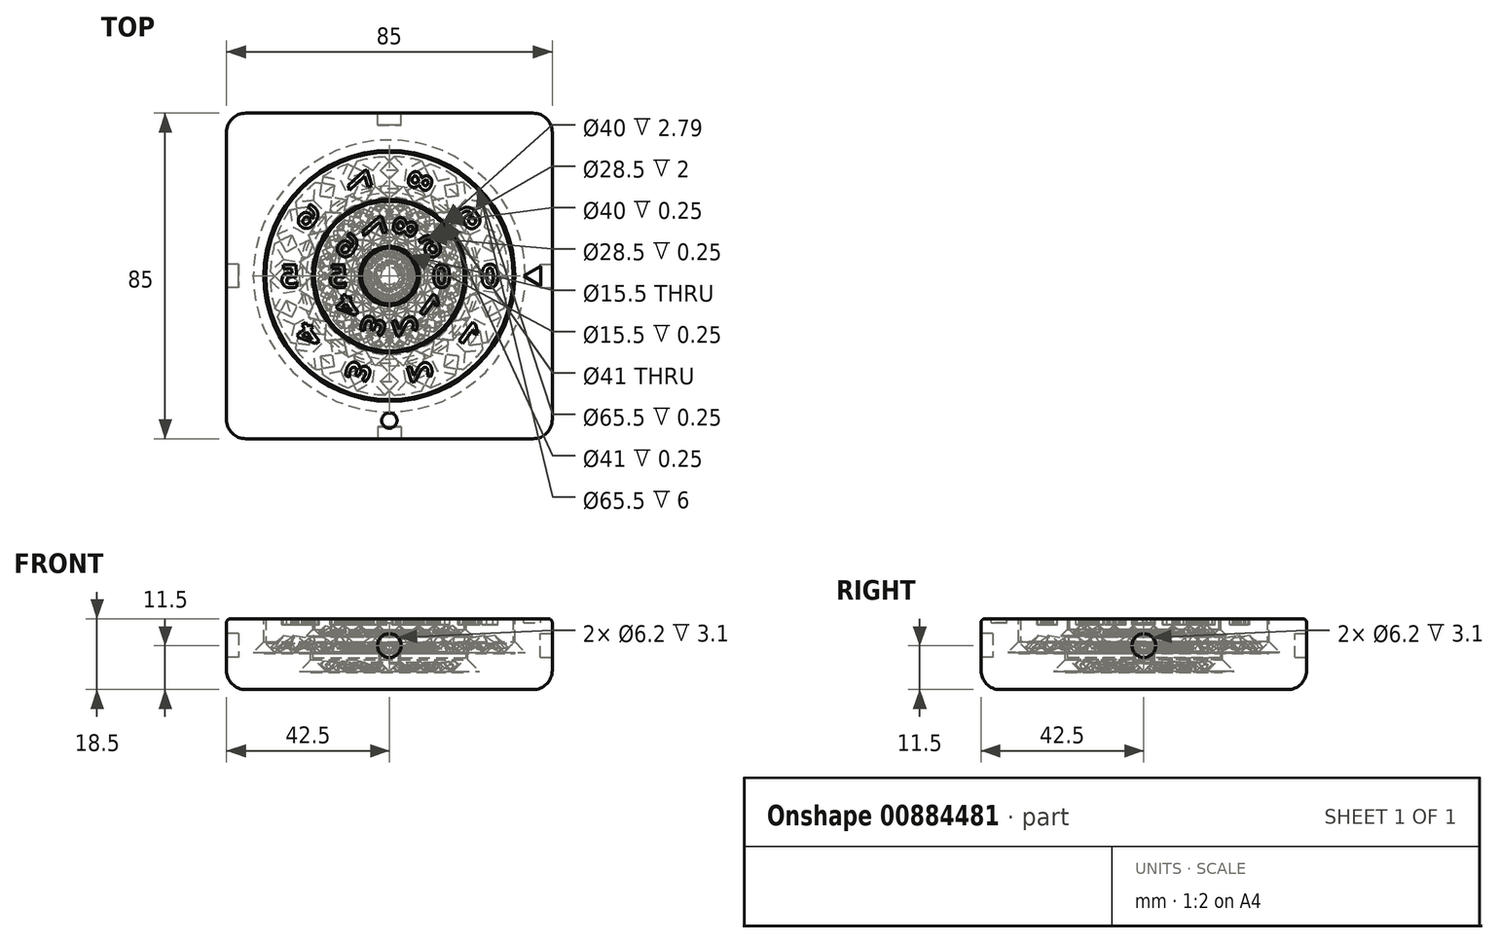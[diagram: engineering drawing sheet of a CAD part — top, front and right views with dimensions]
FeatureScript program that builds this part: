
annotation { "Feature Type Name" : "Feature", "Feature Type Description" : "" }
export const myFeature = defineFeature(function(context is Context, id is Id, definition is map)
    precondition{}
    {
        {
            var Q0;
            Q0=qCreatedBy(makeId("Top.planeOp"),FACE);
            var sketch = newSketch(context, id + "F0", { "sketchPlane" : qUnion([Q0])});
            skLineSegment(sketch, "E0.bottom", {"start": v(-42.5, 42.5) * mm, "end": v(42.5, 42.5) * mm});
            skLineSegment(sketch, "E0.top", {"start": v(-42.5, -42.5) * mm, "end": v(42.5, -42.5) * mm});
            skLineSegment(sketch, "E0.left", {"start": v(-42.5, 42.5) * mm, "end": v(-42.5, -42.5) * mm});
            skLineSegment(sketch, "E0.right", {"start": v(42.5, 42.5) * mm, "end": v(42.5, -42.5) * mm});
            skLineSegment(sketch, "E1", {"start": v(-42.5, 0) * mm, "end": v(42.5, 0) * mm, "construction": true});
            skLineSegment(sketch, "E2", {"start": v(0, -42.5) * mm, "end": v(0, 42.5) * mm, "construction": true});
            skCircle(sketch, "E3", {"center": v(0, -37.75) * mm, "radius": 2 * mm});
            skCircle(sketch, "E4", {"center": v(0, 0) * mm, "radius": 32.75 * mm});
            skCircle(sketch, "E5", {"center": v(0, 0) * mm, "radius": 20.5 * mm});
            skSolve(sketch);
        }
        {
            assignVariable(context, id + "F1", {"name" : "h", "anyValue" : 18.5});
        }
        {
            assignVariable(context, id + "F2", {"name" : "d", "anyValue" : 14});
        }
        {
            var Q0;
            Q0=makeQuery(id+"F0.imprint","IMPRINT",FACE,{"disambiguationData":[TD([[makeQuery(id+"F0.imprint","IMPRINT",EDGE,{"derivedFrom":sQuery(id+"F0.wireOp",EDGE,"TAnjNuv1-8zZz-IdIO-9YnW-rZbYslCo22iK.bottom")}),-1.0]])]});
            var Q1;
            Q1=makeQuery(id+"F0.imprint","IMPRINT",FACE,{"disambiguationData":[TD([[makeQuery(id+"F0.imprint","IMPRINT",EDGE,{"derivedFrom":sQuery(id+"F0.wireOp",EDGE,"E0.bottom")}),-1.0]])]});
            var Q2;
            Q2=makeQuery(id+"F0.imprint","IMPRINT",FACE,{"disambiguationData":[TD([[makeQuery(id+"F0.imprint","IMPRINT",EDGE,{"derivedFrom":sQuery(id+"F0.wireOp",EDGE,"2ee7e992-b2ee-4d81-b33c-59d4d4482344.0.2.0")}),1.0]])]});
            var Q3;
            Q3=makeQuery(id+"F0.imprint","IMPRINT",FACE,{"disambiguationData":[TD([[makeQuery(id+"F0.imprint","IMPRINT",EDGE,{"derivedFrom":sQuery(id+"F0.wireOp",EDGE,"2ee7e992-b2ee-4d81-b33c-59d4d4482344.0.3.0")}),1.0]])]});
            var Q4;
            Q4=makeQuery(id+"F0.imprint","IMPRINT",FACE,{"disambiguationData":[TD([[makeQuery(id+"F0.imprint","IMPRINT",EDGE,{"derivedFrom":sQuery(id+"F0.wireOp",EDGE,"2ee7e992-b2ee-4d81-b33c-59d4d4482344.0.1.0")}),1.0]])]});
            var Q5;
            Q5=makeQuery(id+"F0.imprint","IMPRINT",FACE,{"disambiguationData":[TD([[makeQuery(id+"F0.imprint","IMPRINT",EDGE,{"derivedFrom":sQuery(id+"F0.wireOp",EDGE,"f406dc69-17c4-4892-9ae8-b8d3958ef0eb.0.1.2")}),1.0]])]});
            var Q6;
            Q6=makeQuery(id+"F0.imprint","IMPRINT",FACE,{"disambiguationData":[TD([[makeQuery(id+"F0.imprint","IMPRINT",EDGE,{"derivedFrom":sQuery(id+"F0.wireOp",EDGE,"f406dc69-17c4-4892-9ae8-b8d3958ef0eb.0.2.2")}),1.0]])]});
            var Q7;
            Q7=makeQuery(id+"F0.imprint","IMPRINT",FACE,{"disambiguationData":[TD([[makeQuery(id+"F0.imprint","IMPRINT",EDGE,{"derivedFrom":sQuery(id+"F0.wireOp",EDGE,"f406dc69-17c4-4892-9ae8-b8d3958ef0eb.0.3.2")}),1.0]])]});
            var Q8;
            Q8=makeQuery(id+"F0.imprint","IMPRINT",FACE,{"disambiguationData":[TD([[makeQuery(id+"F0.imprint","IMPRINT",EDGE,{"derivedFrom":sQuery(id+"F0.wireOp",EDGE,"E3")}),1.0]])]});
            var Q9;
            Q9=makeQuery(id+"F0.imprint","IMPRINT",FACE,{"disambiguationData":[TD([[makeQuery(id+"F0.imprint","IMPRINT",EDGE,{"derivedFrom":sQuery(id+"F0.wireOp",EDGE,"E4")}),1.0]])]});
            var Q10;
            Q10=makeQuery(id+"F0.imprint","IMPRINT",FACE,{"disambiguationData":[TD([[makeQuery(id+"F0.imprint","IMPRINT",EDGE,{"derivedFrom":sQuery(id+"F0.wireOp",EDGE,"E5")}),1.0]])]});
            extrude(context, id + "F3", {"entities" : qUnion([Q0, Q1, Q2, Q3, Q4, Q5, Q6, Q7, Q8, Q9, Q10]), "depth" : (getVariable(context, 'h')) * mm, "offsetDistance" : 25 * mm});
        }
        {
            var Q0;
            Q0=makeQuery(id+"F0.imprint","IMPRINT",FACE,{"disambiguationData":[TD([[makeQuery(id+"F0.imprint","IMPRINT",EDGE,{"derivedFrom":sQuery(id+"F0.wireOp",EDGE,"E4")}),1.0]])]});
            extrude(context, id + "F4", {"entities" : qUnion([Q0]), "operationType" : NewBodyOperationType.REMOVE, "depth" : (getVariable(context, 'd') - 5) * mm, "offsetDistance" : 25 * mm});
        }
        {
            var Q0;
            Q0=makeQuery(id+"F0.imprint","IMPRINT",FACE,{"disambiguationData":[TD([[makeQuery(id+"F0.imprint","IMPRINT",EDGE,{"derivedFrom":sQuery(id+"F0.wireOp",EDGE,"E5")}),1.0]])]});
            extrude(context, id + "F5", {"entities" : qUnion([Q0]), "operationType" : NewBodyOperationType.REMOVE, "depth" : (getVariable(context, 'd')) * mm, "offsetDistance" : 25 * mm});
        }
        {
            var Q0;
            Q0=makeQuery(id+"F3.opExtrude","CAP_FACE",FACE,{"disambiguationData":[OSD([sQuery(id+"F0.wireOp",EDGE,"E0.bottom"),sQuery(id+"F0.wireOp",EDGE,"E0.top"),sQuery(id+"F0.wireOp",EDGE,"E0.left"),sQuery(id+"F0.wireOp",EDGE,"E0.right")])],"isStart":false});
            var Q1;
            Q1=makeQuery(id+"F3.opExtrude","SWEPT_EDGE",EDGE,{"disambiguationData":[OSD([sQuery(id+"F0.wireOp",EDGE,"E0.bottom"),sQuery(id+"F0.wireOp",EDGE,"E0.right")])]});
            var Q2;
            Q2=makeQuery(id+"F3.opExtrude","SWEPT_EDGE",EDGE,{"disambiguationData":[OSD([sQuery(id+"F0.wireOp",EDGE,"E0.bottom"),sQuery(id+"F0.wireOp",EDGE,"E0.left")])]});
            var Q3;
            Q3=makeQuery(id+"F3.opExtrude","SWEPT_EDGE",EDGE,{"disambiguationData":[OSD([sQuery(id+"F0.wireOp",EDGE,"E0.top"),sQuery(id+"F0.wireOp",EDGE,"E0.left")])]});
            var Q4;
            Q4=makeQuery(id+"F3.opExtrude","SWEPT_EDGE",EDGE,{"disambiguationData":[OSD([sQuery(id+"F0.wireOp",EDGE,"E0.top"),sQuery(id+"F0.wireOp",EDGE,"E0.right")])]});
            fillet(context, id + "F6", {"entities" : qUnion([Q0, Q1, Q2, Q3, Q4]), "radius" : 5 * mm, "tangentPropagation" : true, "allowEdgeOverflow" : false});
        }
        {
            var Q0;
            Q0=makeQuery(id+"F3.opExtrude","CAP_EDGE",EDGE,{"disambiguationData":[OSD([sQuery(id+"F0.wireOp",EDGE,"E0.left")])],"isStart":true});
            fillet(context, id + "F7", {"entities" : qUnion([Q0]), "radius" : 1 * mm, "tangentPropagation" : true, "allowEdgeOverflow" : false});
        }
        {
            var Q0;
            Q0=makeQuery(id+"F3.opExtrude","SWEPT_FACE",FACE,{"disambiguationData":[OSD([sQuery(id+"F0.wireOp",EDGE,"E0.top")])]});
            var sketch = newSketch(context, id + "F8", { "sketchPlane" : qUnion([Q0])});
            skCircle(sketch, "E6", {"center": v(0, 7) * mm, "radius": 3.1 * mm});
            skSolve(sketch);
        }
        {
            var Q0;
            Q0=makeQuery(id+"F8.imprint","IMPRINT",FACE,{"disambiguationData":[TD([[makeQuery(id+"F8.imprint","IMPRINT",EDGE,{"derivedFrom":sQuery(id+"F8.wireOp",EDGE,"E6")}),1.0]])]});
            extrude(context, id + "F9", {"entities" : qUnion([Q0]), "operationType" : NewBodyOperationType.REMOVE, "oppositeDirection" : true, "depth" : 3.1 * mm, "offsetDistance" : 25 * mm});
        }
        {
            var Q0;
            Q0=makeQuery(id+"F3.opExtrude","SWEPT_FACE",FACE,{"disambiguationData":[OSD([sQuery(id+"F0.wireOp",EDGE,"E0.bottom")])]});
            var sketch = newSketch(context, id + "F10", { "sketchPlane" : qUnion([Q0])});
            skCircle(sketch, "E7", {"center": v(0, 7) * mm, "radius": 3.1 * mm});
            skSolve(sketch);
        }
        {
            var Q0;
            Q0=makeQuery(id+"F10.imprint","IMPRINT",FACE,{"disambiguationData":[TD([[makeQuery(id+"F10.imprint","IMPRINT",EDGE,{"derivedFrom":sQuery(id+"F10.wireOp",EDGE,"E7")}),1.0]])]});
            extrude(context, id + "F11", {"entities" : qUnion([Q0]), "operationType" : NewBodyOperationType.REMOVE, "oppositeDirection" : true, "depth" : 3.1 * mm, "offsetDistance" : 25 * mm});
        }
        {
            var Q0;
            Q0=makeQuery(id+"F3.opExtrude","SWEPT_FACE",FACE,{"disambiguationData":[OSD([sQuery(id+"F0.wireOp",EDGE,"E0.left")])]});
            var sketch = newSketch(context, id + "F12", { "sketchPlane" : qUnion([Q0])});
            skCircle(sketch, "E8", {"center": v(0, 7) * mm, "radius": 3.1 * mm});
            skSolve(sketch);
        }
        {
            var Q0;
            Q0=makeQuery(id+"F12.imprint","IMPRINT",FACE,{"disambiguationData":[TD([[makeQuery(id+"F12.imprint","IMPRINT",EDGE,{"derivedFrom":sQuery(id+"F12.wireOp",EDGE,"E8")}),1.0]])]});
            extrude(context, id + "F13", {"entities" : qUnion([Q0]), "operationType" : NewBodyOperationType.REMOVE, "oppositeDirection" : true, "depth" : 3.1 * mm, "offsetDistance" : 25 * mm});
        }
        {
            var Q0;
            Q0=makeQuery(id+"F3.opExtrude","SWEPT_FACE",FACE,{"disambiguationData":[OSD([sQuery(id+"F0.wireOp",EDGE,"E0.right")])]});
            var sketch = newSketch(context, id + "F14", { "sketchPlane" : qUnion([Q0])});
            skCircle(sketch, "E9", {"center": v(0, 7) * mm, "radius": 3.1 * mm});
            skSolve(sketch);
        }
        {
            var Q0;
            Q0=makeQuery(id+"F14.imprint","IMPRINT",FACE,{"disambiguationData":[TD([[makeQuery(id+"F14.imprint","IMPRINT",EDGE,{"derivedFrom":sQuery(id+"F14.wireOp",EDGE,"E9")}),1.0]])]});
            extrude(context, id + "F15", {"entities" : qUnion([Q0]), "operationType" : NewBodyOperationType.REMOVE, "oppositeDirection" : true, "depth" : 3.1 * mm, "offsetDistance" : 25 * mm});
        }
        {
            var Q0;
            Q0=makeQuery(id+"F0.imprint","IMPRINT",FACE,{"disambiguationData":[TD([[makeQuery(id+"F0.imprint","IMPRINT",EDGE,{"derivedFrom":sQuery(id+"F0.wireOp",EDGE,"E3")}),1.0]])]});
            var Q1;
            Q1=sQuery(id+"F0.wireOp",EDGE,"E3");
            extrude(context, id + "F16", {"entities" : qUnion([Q0]), "operationType" : NewBodyOperationType.REMOVE, "surfaceEntities" : qUnion([Q1]), "depth" : 1 * mm, "offsetDistance" : 25 * mm});
        }
        {
            var Q0;
            Q0=qCreatedBy(makeId("Front.planeOp"),FACE);
            var sketch = newSketch(context, id + "F17", { "sketchPlane" : qUnion([Q0])});
            skLineSegment(sketch, "E10", {"start": v(0, 13.75) * mm, "end": v(0, 8.75) * mm, "construction": true});
            skLineSegment(sketch, "E11", {"start": v(-20, 0) * mm, "end": v(-32.25, 0) * mm});
            skLineSegment(sketch, "E12", {"start": v(-32.25, 0) * mm, "end": v(-32.25, 8.75) * mm});
            skLineSegment(sketch, "E13", {"start": v(-32.25, 8.75) * mm, "end": v(-20, 8.75) * mm});
            skLineSegment(sketch, "E14", {"start": v(-20, 8.75) * mm, "end": v(-20, 13.75) * mm});
            skLineSegment(sketch, "E15", {"start": v(-20, 13.75) * mm, "end": v(-2.75, 13.75) * mm});
            skPoint(sketch, "E16.visualSharp", {"position": v(-20, 13.75) * mm});
            skPoint(sketch, "E17.visualSharp", {"position": v(-32.25, 8.75) * mm});
            skPoint(sketch, "E18.visualSharp", {"position": v(-20, 8.75) * mm});
            skPoint(sketch, "E19.orphan", {"position": v(0, 28.15) * mm});
            skLineSegment(sketch, "E20", {"start": v(-20, 0) * mm, "end": v(-20, 4.75) * mm});
            skLineSegment(sketch, "E21", {"start": v(-20, 4.75) * mm, "end": v(-14.25, 4.75) * mm});
            skLineSegment(sketch, "E22", {"start": v(-14.25, 4.75) * mm, "end": v(-14.25, 8.75) * mm});
            skLineSegment(sketch, "E23", {"start": v(-14.25, 8.75) * mm, "end": v(-2.75, 8.75) * mm});
            skPoint(sketch, "E24.visualSharp", {"position": v(-14.25, 8.75) * mm});
            skPoint(sketch, "E25.visualSharp", {"position": v(-14.25, 4.75) * mm});
            skPoint(sketch, "E26.visualSharp", {"position": v(-20, 4.75) * mm});
            skLineSegment(sketch, "E27", {"start": v(-2.75, 13.75) * mm, "end": v(-2.75, 8.75) * mm});
            skSolve(sketch);
        }
        {
            var Q0;
            Q0=makeQuery(id+"F17.imprint","IMPRINT",FACE,{"disambiguationData":[TD([[makeQuery(id+"F17.imprint","IMPRINT",EDGE,{"derivedFrom":sQuery(id+"F17.wireOp",EDGE,"E11")}),-1.0]])]});
            var Q1;
            Q1=qConstructionFilter(qBodyType(qCreatedBy(id+"F17",EDGE),BodyType.WIRE),ConstructionObject.NO);
            var Q2;
            Q2=sQuery(id+"F17.wireOp",EDGE,"E10");
            revolve(context, id + "F18", {"surfaceOperationType" : NewSurfaceOperationType.NEW, "entities" : qUnion([Q0]), "surfaceEntities" : qUnion([Q1]), "axis" : qUnion([Q2]), "revolveType" : RevolveType.FULL});
        }
        {
            var Q0;
            Q0=qCreatedBy(makeId("Front.planeOp"),FACE);
            var sketch = newSketch(context, id + "F19", { "sketchPlane" : qUnion([Q0])});
            skLineSegment(sketch, "E28", {"start": v(-2.75, 8.5) * mm, "end": v(-13.75, 8.5) * mm});
            skLineSegment(sketch, "E29", {"start": v(-13.75, 8.5) * mm, "end": v(-13.75, 4.5) * mm});
            skLineSegment(sketch, "E30", {"start": v(-13.75, 4.5) * mm, "end": v(-19.5, 4.5) * mm});
            skLineSegment(sketch, "E31", {"start": v(-19.5, 4.5) * mm, "end": v(-19.5, 0) * mm});
            skLineSegment(sketch, "E32", {"start": v(-19.5, 0) * mm, "end": v(-7.75, 0) * mm});
            skLineSegment(sketch, "E33", {"start": v(-7.75, 0) * mm, "end": v(-7.75, 4.5) * mm});
            skLineSegment(sketch, "E34", {"start": v(-7.75, 4.5) * mm, "end": v(-2.75, 4.5) * mm});
            skLineSegment(sketch, "E35", {"start": v(-2.75, 4.5) * mm, "end": v(-2.75, 8.5) * mm});
            skPoint(sketch, "E36.orphan", {"position": v(0, 8.5) * mm});
            skLineSegment(sketch, "E37", {"start": v(0, 19.44) * mm, "end": v(0, -7.38) * mm, "construction": true});
            skSolve(sketch);
        }
        {
            var Q0;
            Q0=makeQuery(id+"F19.imprint","IMPRINT",FACE,{"disambiguationData":[TD([[makeQuery(id+"F19.imprint","IMPRINT",EDGE,{"derivedFrom":sQuery(id+"F19.wireOp",EDGE,"E28")}),1.0]])]});
            var Q1;
            Q1=sQuery(id+"F19.wireOp",EDGE,"E37");
            revolve(context, id + "F20", {"surfaceOperationType" : NewSurfaceOperationType.NEW, "entities" : qUnion([Q0]), "axis" : qUnion([Q1]), "revolveType" : RevolveType.FULL});
        }
        {
            var Q0;
            Q0=makeQuery(id+"F0.imprint","IMPRINT",FACE,{"disambiguationData":[TD([[makeQuery(id+"F0.imprint","IMPRINT",EDGE,{"derivedFrom":sQuery(id+"F0.wireOp",EDGE,"E0.bottom")}),-1.0]])]});
            var sketch = newSketch(context, id + "F21", { "sketchPlane" : qUnion([Q0])});
            skLineSegment(sketch, "E38", {"start": v(0, 0) * mm, "end": v(13.5, 0) * mm, "construction": true});
            skLineSegment(sketch, "E39.1.0", {"start": v(0, 0) * mm, "end": v(32.76, 23.8) * mm, "construction": true});
            skLineSegment(sketch, "E39.2.0", {"start": v(0, 0) * mm, "end": v(12.51, 38.5) * mm, "construction": true});
            skLineSegment(sketch, "E39.3.0", {"start": v(0, 0) * mm, "end": v(-12.51, 38.5) * mm, "construction": true});
            skLineSegment(sketch, "E39.4.0", {"start": v(0, 0) * mm, "end": v(-32.76, 23.8) * mm, "construction": true});
            skLineSegment(sketch, "E39.5.0", {"start": v(0, 0) * mm, "end": v(-13.5, 0) * mm, "construction": true});
            skLineSegment(sketch, "E39.6.0", {"start": v(0, 0) * mm, "end": v(-21.14, -15.36) * mm, "construction": true});
            skLineSegment(sketch, "E39.7.0", {"start": v(0, 0) * mm, "end": v(-12.51, -38.5) * mm, "construction": true});
            skLineSegment(sketch, "E39.8.0", {"start": v(0, 0) * mm, "end": v(8.07, -24.85) * mm, "construction": true});
            skLineSegment(sketch, "E39.9.0", {"start": v(0, 0) * mm, "end": v(21.14, -15.36) * mm, "construction": true});
            skPoint(sketch, "E39.center", {"position": v(0, 0) * mm});
            skCircle(sketch, "E40", {"center": v(0, 0) * mm, "radius": 32.5 * mm, "construction": true});
            skCircle(sketch, "E41", {"center": v(0, 0) * mm, "radius": 19.75 * mm, "construction": true});
            skText(sketch, "E42", { "text": "0", "fontName": "OpenSans-Bold.ttf"});
            skLineSegment(sketch, "E43", {"start": v(-26.12, 0) * mm, "end": v(-28.62, 0) * mm, "construction": true});
            skLineSegment(sketch, "E44", {"start": v(-21.14, -15.36) * mm, "end": v(-32.76, -23.8) * mm, "construction": true});
            skArc(sketch, "E45", {"start": v(-21.14, 15.36) * mm, "mid": v(-24.85, -8.07) * mm, "end": v(-8.07, -24.85) * mm, "construction": true});
            skArc(sketch, "E46", {"start": v(-8.07, 24.85) * mm, "mid": v(-15.36, 21.14) * mm, "end": v(-21.14, 15.36) * mm, "construction": true});
            skArc(sketch, "E47", {"start": v(8.07, 24.85) * mm, "mid": v(0, 26.12) * mm, "end": v(-8.07, 24.85) * mm, "construction": true});
            skArc(sketch, "E48", {"start": v(21.14, 15.36) * mm, "mid": v(15.36, 21.14) * mm, "end": v(8.07, 24.85) * mm, "construction": true});
            skArc(sketch, "E49", {"start": v(26.12, 0) * mm, "mid": v(24.85, 8.07) * mm, "end": v(21.14, 15.36) * mm, "construction": true});
            skLineSegment(sketch, "E50", {"start": v(21.14, -15.36) * mm, "end": v(32.76, -23.8) * mm, "construction": true});
            skLineSegment(sketch, "E51", {"start": v(8.07, -24.85) * mm, "end": v(12.51, -38.5) * mm, "construction": true});
            skArc(sketch, "E52", {"start": v(-8.07, -24.85) * mm, "mid": v(15.36, -21.14) * mm, "end": v(26.12, 0) * mm, "construction": true});
            skText(sketch, "E53", { "text": "1", "fontName": "OpenSans-Bold.ttf"});
            skLineSegment(sketch, "E54", {"start": v(-21.14, -15.36) * mm, "end": v(-22.75, -16.53) * mm, "construction": true});
            skText(sketch, "E55", { "text": "2", "fontName": "OpenSans-Bold.ttf"});
            skLineSegment(sketch, "E56", {"start": v(-8.07, -24.85) * mm, "end": v(-8.85, -27.24) * mm, "construction": true});
            skText(sketch, "E57", { "text": "3", "fontName": "OpenSans-Bold.ttf"});
            skLineSegment(sketch, "E58", {"start": v(8.07, -24.85) * mm, "end": v(8.84, -27.21) * mm, "construction": true});
            skText(sketch, "E59", { "text": "4", "fontName": "OpenSans-Bold.ttf"});
            skLineSegment(sketch, "E60", {"start": v(23.23, -16.87) * mm, "end": v(21.14, -15.36) * mm, "construction": true});
            skText(sketch, "E61", { "text": "5\n", "fontName": "OpenSans-Bold.ttf"});
            skLineSegment(sketch, "E62", {"start": v(26.13, 0) * mm, "end": v(23.66, 0) * mm, "construction": true});
            skText(sketch, "E63", { "text": "6\n", "fontName": "OpenSans-Bold.ttf"});
            skLineSegment(sketch, "E64", {"start": v(21.14, 15.36) * mm, "end": v(23.17, 16.83) * mm, "construction": true});
            skText(sketch, "E65", { "text": "7", "fontName": "OpenSans-Bold.ttf"});
            skLineSegment(sketch, "E66", {"start": v(8.07, 24.85) * mm, "end": v(8.85, 27.24) * mm, "construction": true});
            skText(sketch, "E67", { "text": "8", "fontName": "OpenSans-Bold.ttf"});
            skLineSegment(sketch, "E68", {"start": v(-8.85, 27.23) * mm, "end": v(-8.07, 24.85) * mm, "construction": true});
            skText(sketch, "E69", { "text": "9", "fontName": "OpenSans-Bold.ttf"});
            skLineSegment(sketch, "E70", {"start": v(-23.16, 16.83) * mm, "end": v(-21.14, 15.36) * mm, "construction": true});
            skText(sketch, "E71", { "text": "5\n", "fontName": "OpenSans-Bold.ttf"});
            skLineSegment(sketch, "E72", {"start": v(13.5, 0) * mm, "end": v(11.04, 0) * mm, "construction": true});
            skCircle(sketch, "E73", {"center": v(0, 0) * mm, "radius": 7.5 * mm, "construction": true});
            skCircle(sketch, "E74", {"center": v(0, 0) * mm, "radius": 19.5 * mm, "construction": true});
            skLineSegment(sketch, "E75", {"start": v(13.5, 0) * mm, "end": v(40.49, 0) * mm, "construction": true});
            skArc(sketch, "E76", {"start": v(10.92, 7.94) * mm, "mid": v(7.94, 10.92) * mm, "end": v(4.17, 12.84) * mm, "construction": true});
            skArc(sketch, "E77", {"start": v(10.92, -7.94) * mm, "mid": v(13.5, 0) * mm, "end": v(10.92, 7.94) * mm, "construction": true});
            skArc(sketch, "E78", {"start": v(4.17, -12.84) * mm, "mid": v(7.94, -10.92) * mm, "end": v(10.92, -7.94) * mm, "construction": true});
            skArc(sketch, "E79", {"start": v(-4.17, -12.84) * mm, "mid": v(0, -13.5) * mm, "end": v(4.17, -12.84) * mm, "construction": true});
            skArc(sketch, "E80", {"start": v(4.17, 12.84) * mm, "mid": v(0, 13.5) * mm, "end": v(-4.17, 12.84) * mm, "construction": true});
            skArc(sketch, "E81", {"start": v(-4.17, 12.84) * mm, "mid": v(-7.94, 10.92) * mm, "end": v(-10.92, 7.94) * mm, "construction": true});
            skArc(sketch, "E82", {"start": v(-10.92, 7.94) * mm, "mid": v(-13.5, 0) * mm, "end": v(-10.92, -7.94) * mm, "construction": true});
            skLineSegment(sketch, "E83", {"start": v(-13.5, 0) * mm, "end": v(-40.49, 0) * mm, "construction": true});
            skArc(sketch, "E84", {"start": v(-10.92, -7.94) * mm, "mid": v(-7.94, -10.92) * mm, "end": v(-4.17, -12.84) * mm, "construction": true});
            skText(sketch, "E85", { "text": "6\n", "fontName": "OpenSans-Bold.ttf"});
            skLineSegment(sketch, "E86", {"start": v(10.92, 7.94) * mm, "end": v(12.96, 9.41) * mm, "construction": true});
            skText(sketch, "E87", { "text": "7", "fontName": "OpenSans-Bold.ttf"});
            skLineSegment(sketch, "E88", {"start": v(4.17, 12.84) * mm, "end": v(4.95, 15.23) * mm, "construction": true});
            skText(sketch, "E89", { "text": "8", "fontName": "OpenSans-Bold.ttf"});
            skLineSegment(sketch, "E90", {"start": v(-4.95, 15.22) * mm, "end": v(-4.17, 12.84) * mm, "construction": true});
            skText(sketch, "E91", { "text": "9", "fontName": "OpenSans-Bold.ttf"});
            skLineSegment(sketch, "E92", {"start": v(-12.95, 9.4) * mm, "end": v(-10.92, 7.94) * mm, "construction": true});
            skText(sketch, "E93", { "text": "0", "fontName": "OpenSans-Bold.ttf"});
            skLineSegment(sketch, "E94", {"start": v(-13.5, 0) * mm, "end": v(-16, 0) * mm, "construction": true});
            skText(sketch, "E95", { "text": "1", "fontName": "OpenSans-Bold.ttf"});
            skLineSegment(sketch, "E96", {"start": v(-10.92, -7.94) * mm, "end": v(-12.53, -9.1) * mm, "construction": true});
            skText(sketch, "E97", { "text": "2", "fontName": "OpenSans-Bold.ttf"});
            skLineSegment(sketch, "E98", {"start": v(-4.17, -12.84) * mm, "end": v(-4.95, -15.23) * mm, "construction": true});
            skText(sketch, "E99", { "text": "3", "fontName": "OpenSans-Bold.ttf"});
            skLineSegment(sketch, "E100", {"start": v(4.17, -12.84) * mm, "end": v(4.94, -15.2) * mm, "construction": true});
            skText(sketch, "E101", { "text": "4", "fontName": "OpenSans-Bold.ttf"});
            skLineSegment(sketch, "E102", {"start": v(13.01, -9.45) * mm, "end": v(10.92, -7.94) * mm, "construction": true});
            const initialGuessF21  = {"E42": [-0.02862, -0.003, 1, 0, 0.006], "E53": [-0.02098, -0.01895, 0.80902, 0.58779, 0.006], "E55": [-0.006, -0.02817, 0.30902, 0.95106, 0.006], "E57": [0.0117, -0.02629, -0.30902, 0.95106, 0.006], "E59": [0.02499, -0.01445, -0.80902, 0.58779, 0.006], "E61": [0.02366, -0.003, 1, 0, 0.006], "E63": [0.02086, 0.01145, 0.80902, 0.58779, 0.006], "E65": [0.01015, 0.02153, 0.30902, 0.95106, 0.006], "E67": [-0.00445, 0.0234, -0.30902, 0.95106, 0.006], "E69": [-0.01735, 0.01631, -0.80902, 0.58779, 0.006], "E71": [0.01104, -0.003, 1, 0, 0.006], "E85": [0.01065, 0.00403, 0.80902, 0.58779, 0.006], "E87": [0.00625, 0.00952, 0.30902, 0.95106, 0.006], "E89": [-0.00054, 0.01138, -0.30902, 0.95106, 0.006], "E91": [-0.00713, 0.0089, -0.80902, 0.58779, 0.006], "E93": [-0.016, -0.003, 1, 0, 0.006], "E95": [-0.01077, -0.01153, 0.80902, 0.58779, 0.006], "E97": [-0.0021, -0.01616, 0.30902, 0.95106, 0.006], "E99": [0.0078, -0.01428, -0.30902, 0.95106, 0.006], "E101": [0.01478, -0.00703, -0.80902, 0.58779, 0.006]};
            skSetInitialGuess(sketch, initialGuessF21);
            skSolve(sketch);
        }
        {
            var Q0;
            Q0=qSketchRegion(id+"F21",true);
            extrude(context, id + "F22", {"entities" : qUnion([Q0]), "operationType" : NewBodyOperationType.REMOVE, "depth" : 1.5 * mm, "offsetDistance" : 25 * mm});
        }
        {
            var Q0;
            Q0=qSketchRegion(id+"F21",true);
            extrude(context, id + "F23", {"entities" : qUnion([Q0]), "operationType" : NewBodyOperationType.REMOVE, "depth" : 1.5 * mm, "offsetDistance" : 25 * mm});
        }
        {
            var Q0;
            Q0=qCreatedBy(makeId("Front.planeOp"),FACE);
            var sketch = newSketch(context, id + "F24", { "sketchPlane" : qUnion([Q0])});
            skLineSegment(sketch, "E103", {"start": v(0, 0) * mm, "end": v(7.25, 0) * mm});
            skLineSegment(sketch, "E104", {"start": v(7.25, 0) * mm, "end": v(7.25, 4.25) * mm});
            skLineSegment(sketch, "E105", {"start": v(7.25, 4.25) * mm, "end": v(2.25, 4.25) * mm});
            skLineSegment(sketch, "E106", {"start": v(2.25, 4.25) * mm, "end": v(2.25, 18.5) * mm});
            skLineSegment(sketch, "E107", {"start": v(2.25, 18.5) * mm, "end": v(0, 18.5) * mm});
            skLineSegment(sketch, "E108", {"start": v(0, 18.5) * mm, "end": v(0, 0) * mm});
            skSolve(sketch);
        }
        {
            var Q0;
            Q0=makeQuery(id+"F24.imprint","IMPRINT",FACE,{"disambiguationData":[TD([[makeQuery(id+"F24.imprint","IMPRINT",EDGE,{"derivedFrom":sQuery(id+"F24.wireOp",EDGE,"E103")}),1.0]])]});
            var Q1;
            Q1=sQuery(id+"F24.wireOp",EDGE,"E108");
            revolve(context, id + "F25", {"operationType" : NewBodyOperationType.ADD, "surfaceOperationType" : NewSurfaceOperationType.NEW, "entities" : qUnion([Q0]), "axis" : qUnion([Q1]), "revolveType" : RevolveType.FULL});
        }
        {
            var Q0;
            Q0=makeQuery(id+"F3.opExtrude","SWEPT_BODY",BODY,{"disambiguationData":[OSD([sQuery(id+"F0.wireOp",EDGE,"E0.bottom"),sQuery(id+"F0.wireOp",EDGE,"E0.top"),sQuery(id+"F0.wireOp",EDGE,"E0.left"),sQuery(id+"F0.wireOp",EDGE,"E0.right")])]});
            var Q1;
            Q1=makeQuery(id+"F18.opRevolve","SWEPT_BODY",BODY,{"disambiguationData":[OSD([sQuery(id+"F17.wireOp",EDGE,"E11"),sQuery(id+"F17.wireOp",EDGE,"E12"),sQuery(id+"F17.wireOp",EDGE,"E13"),sQuery(id+"F17.wireOp",EDGE,"E14"),sQuery(id+"F17.wireOp",EDGE,"E15"),sQuery(id+"F17.wireOp",EDGE,"E16.filletArc"),sQuery(id+"F17.wireOp",EDGE,"E17.filletArc"),sQuery(id+"F17.wireOp",EDGE,"E18.filletArc"),sQuery(id+"F17.wireOp",EDGE,"E20"),sQuery(id+"F17.wireOp",EDGE,"E21"),sQuery(id+"F17.wireOp",EDGE,"E22"),sQuery(id+"F17.wireOp",EDGE,"E23"),sQuery(id+"F17.wireOp",EDGE,"E24.filletArc"),sQuery(id+"F17.wireOp",EDGE,"E25.filletArc"),sQuery(id+"F17.wireOp",EDGE,"E26.filletArc"),sQuery(id+"F17.wireOp",EDGE,"E27")])]});
            var Q2;
            Q2=makeQuery(id+"F20.opRevolve","SWEPT_BODY",BODY,{"disambiguationData":[OSD([sQuery(id+"F19.wireOp",EDGE,"E28"),sQuery(id+"F19.wireOp",EDGE,"E29"),sQuery(id+"F19.wireOp",EDGE,"E30"),sQuery(id+"F19.wireOp",EDGE,"E31"),sQuery(id+"F19.wireOp",EDGE,"E32"),sQuery(id+"F19.wireOp",EDGE,"E33"),sQuery(id+"F19.wireOp",EDGE,"E34"),sQuery(id+"F19.wireOp",EDGE,"E35"),sQuery(id+"F19.wireOp",EDGE,"caf7a765-5534-4870-827b-03466f1c99e3.filletArc"),sQuery(id+"F19.wireOp",EDGE,"dd2b0f7d-4639-499b-b715-159063f6e088.filletArc"),sQuery(id+"F19.wireOp",EDGE,"7f4fc2b8-c080-4429-a952-9433392ce116.filletArc"),sQuery(id+"F19.wireOp",EDGE,"d3ce06f0-3ce8-42c3-862a-95c5991aedac.filletArc")])]});
            var Q3;
            Q3=sQuery(id+"F0.wireOp",EDGE,"E2");
            var Q4;
            Q4=sQuery(id+"F0.wireOp",EDGE,"E2");
            transform(context, id + "F26", {"entities" : qUnion([Q0, Q1, Q2]), "transformType" : TransformType.ROTATION, "transformAxis" : qUnion([Q4]), "angle" : 180 * degree, "makeCopy" : false});
        }
        {
            var Q0;
            Q0=makeQuery(id+"F25.opRevolve","SWEPT_FACE",FACE,{"disambiguationData":[OSD([sQuery(id+"F24.wireOp",EDGE,"E105")])]});
            var sketch = newSketch(context, id + "F27", { "sketchPlane" : qUnion([Q0])});
            skCircle(sketch, "E109", {"center": v(0, 0) * mm, "radius": 3.62 * mm});
            skCircle(sketch, "E110", {"center": v(0, 0) * mm, "radius": 5.85 * mm});
            skCircle(sketch, "E111", {"center": v(0, 0) * mm, "radius": 8.5 * mm});
            skSolve(sketch);
        }
        {
            var Q0;
            Q0=makeQuery(id+"F18.opRevolve","SWEPT_FACE",FACE,{"disambiguationData":[OSD([sQuery(id+"F17.wireOp",EDGE,"E15")])]});
            var sketch = newSketch(context, id + "F28", { "sketchPlane" : qUnion([Q0])});
            skLineSegment(sketch, "E112", {"start": v(0, 0) * mm, "end": v(32.5, 0) * mm});
            skLineSegment(sketch, "E113.1.0", {"start": v(0, 0) * mm, "end": v(19.04, 6.18) * mm});
            skLineSegment(sketch, "E113.2.0", {"start": v(0, 0) * mm, "end": v(16.2, 11.76) * mm});
            skLineSegment(sketch, "E113.3.0", {"start": v(0, 0) * mm, "end": v(19.1, 26.3) * mm});
            skLineSegment(sketch, "E113.4.0", {"start": v(0, 0) * mm, "end": v(10.04, 30.9) * mm});
            skLineSegment(sketch, "E113.5.0", {"start": v(0, 0) * mm, "end": v(0, 32.5) * mm});
            skLineSegment(sketch, "E113.6.0", {"start": v(0, 0) * mm, "end": v(-10.04, 30.9) * mm});
            skLineSegment(sketch, "E113.7.0", {"start": v(0, 0) * mm, "end": v(-19.1, 26.3) * mm});
            skLineSegment(sketch, "E113.8.0", {"start": v(0, 0) * mm, "end": v(-26.3, 19.1) * mm});
            skLineSegment(sketch, "E113.9.0", {"start": v(0, 0) * mm, "end": v(-19.04, 6.18) * mm});
            skLineSegment(sketch, "E113.10.0", {"start": v(0, 0) * mm, "end": v(-32.5, 0) * mm});
            skLineSegment(sketch, "E113.11.0", {"start": v(0, 0) * mm, "end": v(-30.9, -10.04) * mm});
            skLineSegment(sketch, "E113.12.0", {"start": v(0, 0) * mm, "end": v(-16.2, -11.76) * mm});
            skLineSegment(sketch, "E113.13.0", {"start": v(0, 0) * mm, "end": v(-19.1, -26.3) * mm});
            skLineSegment(sketch, "E113.14.0", {"start": v(0, 0) * mm, "end": v(-6.18, -19.04) * mm});
            skLineSegment(sketch, "E113.15.0", {"start": v(0, 0) * mm, "end": v(0, -20.01) * mm});
            skLineSegment(sketch, "E113.16.0", {"start": v(0, 0) * mm, "end": v(6.18, -19.04) * mm});
            skLineSegment(sketch, "E113.17.0", {"start": v(0, 0) * mm, "end": v(19.1, -26.3) * mm});
            skLineSegment(sketch, "E113.18.0", {"start": v(0, 0) * mm, "end": v(16.2, -11.76) * mm});
            skLineSegment(sketch, "E113.19.0", {"start": v(0, 0) * mm, "end": v(30.9, -10.04) * mm});
            skPoint(sketch, "E113.center", {"position": v(0, 0) * mm});
            skCircle(sketch, "E114", {"center": v(0, 0) * mm, "radius": 32.5 * mm});
            skArc(sketch, "E115", {"start": v(-16.2, 11.76) * mm, "mid": v(-19.04, 6.18) * mm, "end": v(-20.01, 0) * mm});
            skArc(sketch, "E116", {"start": v(-11.76, 16.2) * mm, "mid": v(-14.15, 14.15) * mm, "end": v(-16.2, 11.76) * mm});
            skArc(sketch, "E117", {"start": v(-6.18, 19.04) * mm, "mid": v(-9.09, 17.83) * mm, "end": v(-11.76, 16.2) * mm});
            skArc(sketch, "E118", {"start": v(0, 20.01) * mm, "mid": v(-3.13, 19.77) * mm, "end": v(-6.18, 19.04) * mm});
            skArc(sketch, "E119", {"start": v(6.18, 19.04) * mm, "mid": v(3.13, 19.77) * mm, "end": v(0, 20.01) * mm});
            skArc(sketch, "E120", {"start": v(11.76, 16.2) * mm, "mid": v(9.09, 17.83) * mm, "end": v(6.18, 19.04) * mm});
            skLineSegment(sketch, "E121", {"start": v(16.2, 11.76) * mm, "end": v(26.3, 19.1) * mm});
            skLineSegment(sketch, "E122", {"start": v(19.04, 6.18) * mm, "end": v(30.9, 10.04) * mm});
            skArc(sketch, "E123", {"start": v(20.01, 0) * mm, "mid": v(17.83, 9.09) * mm, "end": v(11.76, 16.2) * mm});
            skArc(sketch, "E124", {"start": v(19.04, -6.18) * mm, "mid": v(19.77, -3.13) * mm, "end": v(20.01, 0) * mm});
            skLineSegment(sketch, "E125", {"start": v(16.2, -11.76) * mm, "end": v(26.3, -19.1) * mm});
            skArc(sketch, "E126", {"start": v(11.76, -16.2) * mm, "mid": v(16.2, -11.76) * mm, "end": v(19.04, -6.18) * mm});
            skLineSegment(sketch, "E127", {"start": v(6.18, -19.04) * mm, "end": v(10.04, -30.9) * mm});
            skLineSegment(sketch, "E128", {"start": v(0, -20.01) * mm, "end": v(0, -32.5) * mm});
            skLineSegment(sketch, "E129", {"start": v(-6.18, -19.04) * mm, "end": v(-10.04, -30.9) * mm});
            skArc(sketch, "E130", {"start": v(-11.76, -16.2) * mm, "mid": v(0, -20.01) * mm, "end": v(11.76, -16.2) * mm});
            skLineSegment(sketch, "E131", {"start": v(-16.2, -11.76) * mm, "end": v(-26.3, -19.1) * mm});
            skArc(sketch, "E132", {"start": v(-19.04, -6.18) * mm, "mid": v(-16.2, -11.76) * mm, "end": v(-11.76, -16.2) * mm});
            skArc(sketch, "E133", {"start": v(-20.01, 0) * mm, "mid": v(-19.77, -3.13) * mm, "end": v(-19.04, -6.18) * mm});
            skLineSegment(sketch, "E134", {"start": v(-19.04, 6.18) * mm, "end": v(-30.9, 10.04) * mm});
            skSolve(sketch);
        }
        {
            var Q0;
            Q0=makeQuery(id+"F18.opRevolve","SWEPT_FACE",FACE,{"disambiguationData":[OSD([sQuery(id+"F17.wireOp",EDGE,"E15")])]});
            var sketch = newSketch(context, id + "F29", { "sketchPlane" : qUnion([Q0])});
            skCircle(sketch, "E135", {"center": v(0, 0) * mm, "radius": 6.74 * mm});
            skCircle(sketch, "E136", {"center": v(0, 0) * mm, "radius": 11.63 * mm});
            skCircle(sketch, "E137", {"center": v(0, 0) * mm, "radius": 16.5 * mm});
            skCircle(sketch, "E138", {"center": v(0, 0) * mm, "radius": 23.5 * mm});
            skSolve(sketch);
        }
        {
            var Q0;
            Q0=makeQuery(id+"F20.opRevolve","SWEPT_FACE",FACE,{"disambiguationData":[OSD([sQuery(id+"F19.wireOp",EDGE,"E28")])]});
            var sketch = newSketch(context, id + "F30", { "sketchPlane" : qUnion([Q0])});
            skCircle(sketch, "E139", {"center": v(0, 0) * mm, "radius": 5.5 * mm});
            skCircle(sketch, "E140", {"center": v(0, 0) * mm, "radius": 11.5 * mm});
            skCircle(sketch, "E141", {"center": v(0, 0) * mm, "radius": 16 * mm});
            skCircle(sketch, "E142", {"center": v(0, 0) * mm, "radius": 8.5 * mm});
            skSolve(sketch);
        }
        {
            var Q0;
            Q0=makeQuery(id+"F20.opRevolve","SWEPT_FACE",FACE,{"disambiguationData":[OSD([sQuery(id+"F19.wireOp",EDGE,"E30")])]});
            var sketch = newSketch(context, id + "F31", { "sketchPlane" : qUnion([Q0])});
            skCircle(sketch, "E143", {"center": v(0, 0) * mm, "radius": 15.84 * mm});
            skCircle(sketch, "E144", {"center": v(0, 0) * mm, "radius": 17.86 * mm});
            skCircle(sketch, "E145", {"center": v(0, 0) * mm, "radius": 21.71 * mm});
            skSolve(sketch);
        }
        {
            var Q0;
            {var subQ0=sQuery(id+"F28.wireOp",EDGE,"E113.11.0");var subQ1=sQuery(id+"F17.wireOp",EDGE,"E15");var subQ2=makeQuery(id+"F18.opRevolve","SWEPT_EDGE",EDGE,{"disambiguationData":[OSD([subQ1,sQuery(id+"F17.wireOp",EDGE,"E27")])]});var subQ3=makeQuery(id+"F28.imprint","INTERSECT",VERTEX,{"derivedFrom":[subQ2,subQ0]});Q0=makeQuery(id+"F28.imprint","IMPRINT",FACE,{"disambiguationData":[TD([[makeQuery(id+"F28.imprint","IMPRINT",EDGE,{"disambiguationData":[TD([[subQ3,-1.0]])],"derivedFrom":subQ0}),1.0]])]});}
            var Q1;
            {var subQ0=sQuery(id+"F28.wireOp",EDGE,"E113.13.0");var subQ1=sQuery(id+"F17.wireOp",EDGE,"E15");var subQ2=makeQuery(id+"F18.opRevolve","SWEPT_EDGE",EDGE,{"disambiguationData":[OSD([subQ1,sQuery(id+"F17.wireOp",EDGE,"E27")])]});var subQ3=makeQuery(id+"F28.imprint","INTERSECT",VERTEX,{"derivedFrom":[subQ2,subQ0]});Q1=makeQuery(id+"F28.imprint","IMPRINT",FACE,{"disambiguationData":[TD([[makeQuery(id+"F28.imprint","IMPRINT",EDGE,{"disambiguationData":[TD([[subQ3,-1.0]])],"derivedFrom":subQ0}),1.0]])]});}
            var Q2;
            {var subQ0=sQuery(id+"F28.wireOp",EDGE,"E113.15.0");var subQ1=sQuery(id+"F17.wireOp",EDGE,"E15");var subQ2=makeQuery(id+"F18.opRevolve","SWEPT_EDGE",EDGE,{"disambiguationData":[OSD([subQ1,sQuery(id+"F17.wireOp",EDGE,"E27")])]});var subQ3=makeQuery(id+"F28.imprint","INTERSECT",VERTEX,{"derivedFrom":[subQ2,subQ0]});Q2=makeQuery(id+"F28.imprint","IMPRINT",FACE,{"disambiguationData":[TD([[makeQuery(id+"F28.imprint","IMPRINT",EDGE,{"disambiguationData":[TD([[subQ3,-1.0]])],"derivedFrom":subQ0}),1.0]])]});}
            var Q3;
            {var subQ0=sQuery(id+"F28.wireOp",EDGE,"E113.17.0");var subQ1=sQuery(id+"F17.wireOp",EDGE,"E15");var subQ2=makeQuery(id+"F18.opRevolve","SWEPT_EDGE",EDGE,{"disambiguationData":[OSD([subQ1,sQuery(id+"F17.wireOp",EDGE,"E27")])]});var subQ3=makeQuery(id+"F28.imprint","INTERSECT",VERTEX,{"derivedFrom":[subQ2,subQ0]});Q3=makeQuery(id+"F28.imprint","IMPRINT",FACE,{"disambiguationData":[TD([[makeQuery(id+"F28.imprint","IMPRINT",EDGE,{"disambiguationData":[TD([[subQ3,-1.0]])],"derivedFrom":subQ0}),1.0]])]});}
            var Q4;
            {var subQ0=sQuery(id+"F28.wireOp",EDGE,"E112");var subQ1=sQuery(id+"F17.wireOp",EDGE,"E15");var subQ2=makeQuery(id+"F18.opRevolve","SWEPT_EDGE",EDGE,{"disambiguationData":[OSD([subQ1,sQuery(id+"F17.wireOp",EDGE,"E27")])]});var subQ3=makeQuery(id+"F28.imprint","INTERSECT",VERTEX,{"derivedFrom":[subQ2,subQ0]});Q4=makeQuery(id+"F28.imprint","IMPRINT",FACE,{"disambiguationData":[TD([[makeQuery(id+"F28.imprint","IMPRINT",EDGE,{"disambiguationData":[TD([[subQ3,-1.0]])],"derivedFrom":subQ0}),-1.0]])]});}
            var Q5;
            {var subQ0=sQuery(id+"F28.wireOp",EDGE,"E113.1.0");var subQ1=sQuery(id+"F17.wireOp",EDGE,"E15");var subQ2=makeQuery(id+"F18.opRevolve","SWEPT_EDGE",EDGE,{"disambiguationData":[OSD([subQ1,sQuery(id+"F17.wireOp",EDGE,"E27")])]});var subQ3=makeQuery(id+"F28.imprint","INTERSECT",VERTEX,{"derivedFrom":[subQ2,subQ0]});Q5=makeQuery(id+"F28.imprint","IMPRINT",FACE,{"disambiguationData":[TD([[makeQuery(id+"F28.imprint","IMPRINT",EDGE,{"disambiguationData":[TD([[subQ3,-1.0]])],"derivedFrom":subQ0}),1.0]])]});}
            var Q6;
            {var subQ0=sQuery(id+"F28.wireOp",EDGE,"E113.3.0");var subQ1=sQuery(id+"F17.wireOp",EDGE,"E15");var subQ2=makeQuery(id+"F18.opRevolve","SWEPT_EDGE",EDGE,{"disambiguationData":[OSD([subQ1,sQuery(id+"F17.wireOp",EDGE,"E27")])]});var subQ3=makeQuery(id+"F28.imprint","INTERSECT",VERTEX,{"derivedFrom":[subQ2,subQ0]});Q6=makeQuery(id+"F28.imprint","IMPRINT",FACE,{"disambiguationData":[TD([[makeQuery(id+"F28.imprint","IMPRINT",EDGE,{"disambiguationData":[TD([[subQ3,-1.0]])],"derivedFrom":subQ0}),1.0]])]});}
            var Q7;
            {var subQ0=sQuery(id+"F28.wireOp",EDGE,"E113.5.0");var subQ1=sQuery(id+"F17.wireOp",EDGE,"E15");var subQ2=makeQuery(id+"F18.opRevolve","SWEPT_EDGE",EDGE,{"disambiguationData":[OSD([subQ1,sQuery(id+"F17.wireOp",EDGE,"E27")])]});var subQ3=makeQuery(id+"F28.imprint","INTERSECT",VERTEX,{"derivedFrom":[subQ2,subQ0]});Q7=makeQuery(id+"F28.imprint","IMPRINT",FACE,{"disambiguationData":[TD([[makeQuery(id+"F28.imprint","IMPRINT",EDGE,{"disambiguationData":[TD([[subQ3,-1.0]])],"derivedFrom":subQ0}),1.0]])]});}
            var Q8;
            {var subQ0=sQuery(id+"F28.wireOp",EDGE,"E113.7.0");var subQ1=sQuery(id+"F17.wireOp",EDGE,"E15");var subQ2=makeQuery(id+"F18.opRevolve","SWEPT_EDGE",EDGE,{"disambiguationData":[OSD([subQ1,sQuery(id+"F17.wireOp",EDGE,"E27")])]});var subQ3=makeQuery(id+"F28.imprint","INTERSECT",VERTEX,{"derivedFrom":[subQ2,subQ0]});Q8=makeQuery(id+"F28.imprint","IMPRINT",FACE,{"disambiguationData":[TD([[makeQuery(id+"F28.imprint","IMPRINT",EDGE,{"disambiguationData":[TD([[subQ3,-1.0]])],"derivedFrom":subQ0}),1.0]])]});}
            var Q9;
            {var subQ0=sQuery(id+"F28.wireOp",EDGE,"E113.9.0");var subQ1=sQuery(id+"F17.wireOp",EDGE,"E15");var subQ2=makeQuery(id+"F18.opRevolve","SWEPT_EDGE",EDGE,{"disambiguationData":[OSD([subQ1,sQuery(id+"F17.wireOp",EDGE,"E27")])]});var subQ3=makeQuery(id+"F28.imprint","INTERSECT",VERTEX,{"derivedFrom":[subQ2,subQ0]});Q9=makeQuery(id+"F28.imprint","IMPRINT",FACE,{"disambiguationData":[TD([[makeQuery(id+"F28.imprint","IMPRINT",EDGE,{"disambiguationData":[TD([[subQ3,-1.0]])],"derivedFrom":subQ0}),1.0]])]});}
            extrude(context, id + "F32", {"entities" : qUnion([Q0, Q1, Q2, Q3, Q4, Q5, Q6, Q7, Q8, Q9]), "operationType" : NewBodyOperationType.REMOVE, "oppositeDirection" : true, "depth" : 25 * mm, "offsetDistance" : 25 * mm, "hasDraft" : true, "draftAngle" : 45 * degree, "draftPullDirection" : true});
        }
        {
            var Q0;
            {var subQ0=sQuery(id+"F28.wireOp",EDGE,"E113.12.0");var subQ1=sQuery(id+"F17.wireOp",EDGE,"E15");var subQ2=makeQuery(id+"F18.opRevolve","SWEPT_EDGE",EDGE,{"disambiguationData":[OSD([subQ1,sQuery(id+"F17.wireOp",EDGE,"E27")])]});var subQ3=makeQuery(id+"F28.imprint","INTERSECT",VERTEX,{"derivedFrom":[subQ2,subQ0]});Q0=makeQuery(id+"F28.imprint","IMPRINT",FACE,{"disambiguationData":[TD([[makeQuery(id+"F28.imprint","IMPRINT",EDGE,{"disambiguationData":[TD([[subQ3,-1.0]])],"derivedFrom":subQ0}),1.0]])]});}
            var Q1;
            {var subQ0=sQuery(id+"F28.wireOp",EDGE,"E113.10.0");var subQ1=sQuery(id+"F17.wireOp",EDGE,"E15");var subQ2=makeQuery(id+"F18.opRevolve","SWEPT_EDGE",EDGE,{"disambiguationData":[OSD([subQ1,sQuery(id+"F17.wireOp",EDGE,"E27")])]});var subQ3=makeQuery(id+"F28.imprint","INTERSECT",VERTEX,{"derivedFrom":[subQ2,subQ0]});Q1=makeQuery(id+"F28.imprint","IMPRINT",FACE,{"disambiguationData":[TD([[makeQuery(id+"F28.imprint","IMPRINT",EDGE,{"disambiguationData":[TD([[subQ3,-1.0]])],"derivedFrom":subQ0}),1.0]])]});}
            var Q2;
            {var subQ0=sQuery(id+"F28.wireOp",EDGE,"E113.8.0");var subQ1=sQuery(id+"F17.wireOp",EDGE,"E15");var subQ2=makeQuery(id+"F18.opRevolve","SWEPT_EDGE",EDGE,{"disambiguationData":[OSD([subQ1,sQuery(id+"F17.wireOp",EDGE,"E27")])]});var subQ3=makeQuery(id+"F28.imprint","INTERSECT",VERTEX,{"derivedFrom":[subQ2,subQ0]});Q2=makeQuery(id+"F28.imprint","IMPRINT",FACE,{"disambiguationData":[TD([[makeQuery(id+"F28.imprint","IMPRINT",EDGE,{"disambiguationData":[TD([[subQ3,-1.0]])],"derivedFrom":subQ0}),1.0]])]});}
            var Q3;
            {var subQ0=sQuery(id+"F28.wireOp",EDGE,"E113.6.0");var subQ1=sQuery(id+"F17.wireOp",EDGE,"E15");var subQ2=makeQuery(id+"F18.opRevolve","SWEPT_EDGE",EDGE,{"disambiguationData":[OSD([subQ1,sQuery(id+"F17.wireOp",EDGE,"E27")])]});var subQ3=makeQuery(id+"F28.imprint","INTERSECT",VERTEX,{"derivedFrom":[subQ2,subQ0]});Q3=makeQuery(id+"F28.imprint","IMPRINT",FACE,{"disambiguationData":[TD([[makeQuery(id+"F28.imprint","IMPRINT",EDGE,{"disambiguationData":[TD([[subQ3,-1.0]])],"derivedFrom":subQ0}),1.0]])]});}
            var Q4;
            {var subQ0=sQuery(id+"F28.wireOp",EDGE,"E113.4.0");var subQ1=sQuery(id+"F17.wireOp",EDGE,"E15");var subQ2=makeQuery(id+"F18.opRevolve","SWEPT_EDGE",EDGE,{"disambiguationData":[OSD([subQ1,sQuery(id+"F17.wireOp",EDGE,"E27")])]});var subQ3=makeQuery(id+"F28.imprint","INTERSECT",VERTEX,{"derivedFrom":[subQ2,subQ0]});Q4=makeQuery(id+"F28.imprint","IMPRINT",FACE,{"disambiguationData":[TD([[makeQuery(id+"F28.imprint","IMPRINT",EDGE,{"disambiguationData":[TD([[subQ3,-1.0]])],"derivedFrom":subQ0}),1.0]])]});}
            var Q5;
            {var subQ0=sQuery(id+"F28.wireOp",EDGE,"E113.2.0");var subQ1=sQuery(id+"F17.wireOp",EDGE,"E15");var subQ2=makeQuery(id+"F18.opRevolve","SWEPT_EDGE",EDGE,{"disambiguationData":[OSD([subQ1,sQuery(id+"F17.wireOp",EDGE,"E27")])]});var subQ3=makeQuery(id+"F28.imprint","INTERSECT",VERTEX,{"derivedFrom":[subQ2,subQ0]});Q5=makeQuery(id+"F28.imprint","IMPRINT",FACE,{"disambiguationData":[TD([[makeQuery(id+"F28.imprint","IMPRINT",EDGE,{"disambiguationData":[TD([[subQ3,-1.0]])],"derivedFrom":subQ0}),1.0]])]});}
            var Q6;
            {var subQ0=sQuery(id+"F28.wireOp",EDGE,"E112");var subQ1=sQuery(id+"F17.wireOp",EDGE,"E15");var subQ2=makeQuery(id+"F18.opRevolve","SWEPT_EDGE",EDGE,{"disambiguationData":[OSD([subQ1,sQuery(id+"F17.wireOp",EDGE,"E27")])]});var subQ3=makeQuery(id+"F28.imprint","INTERSECT",VERTEX,{"derivedFrom":[subQ2,subQ0]});Q6=makeQuery(id+"F28.imprint","IMPRINT",FACE,{"disambiguationData":[TD([[makeQuery(id+"F28.imprint","IMPRINT",EDGE,{"disambiguationData":[TD([[subQ3,-1.0]])],"derivedFrom":subQ0}),1.0]])]});}
            var Q7;
            {var subQ0=sQuery(id+"F28.wireOp",EDGE,"E113.18.0");var subQ1=sQuery(id+"F17.wireOp",EDGE,"E15");var subQ2=makeQuery(id+"F18.opRevolve","SWEPT_EDGE",EDGE,{"disambiguationData":[OSD([subQ1,sQuery(id+"F17.wireOp",EDGE,"E27")])]});var subQ3=makeQuery(id+"F28.imprint","INTERSECT",VERTEX,{"derivedFrom":[subQ2,subQ0]});Q7=makeQuery(id+"F28.imprint","IMPRINT",FACE,{"disambiguationData":[TD([[makeQuery(id+"F28.imprint","IMPRINT",EDGE,{"disambiguationData":[TD([[subQ3,-1.0]])],"derivedFrom":subQ0}),1.0]])]});}
            var Q8;
            {var subQ0=sQuery(id+"F28.wireOp",EDGE,"E113.16.0");var subQ1=sQuery(id+"F17.wireOp",EDGE,"E15");var subQ2=makeQuery(id+"F18.opRevolve","SWEPT_EDGE",EDGE,{"disambiguationData":[OSD([subQ1,sQuery(id+"F17.wireOp",EDGE,"E27")])]});var subQ3=makeQuery(id+"F28.imprint","INTERSECT",VERTEX,{"derivedFrom":[subQ2,subQ0]});Q8=makeQuery(id+"F28.imprint","IMPRINT",FACE,{"disambiguationData":[TD([[makeQuery(id+"F28.imprint","IMPRINT",EDGE,{"disambiguationData":[TD([[subQ3,-1.0]])],"derivedFrom":subQ0}),1.0]])]});}
            var Q9;
            {var subQ0=sQuery(id+"F28.wireOp",EDGE,"E113.14.0");var subQ1=sQuery(id+"F17.wireOp",EDGE,"E15");var subQ2=makeQuery(id+"F18.opRevolve","SWEPT_EDGE",EDGE,{"disambiguationData":[OSD([subQ1,sQuery(id+"F17.wireOp",EDGE,"E27")])]});var subQ3=makeQuery(id+"F28.imprint","INTERSECT",VERTEX,{"derivedFrom":[subQ2,subQ0]});Q9=makeQuery(id+"F28.imprint","IMPRINT",FACE,{"disambiguationData":[TD([[makeQuery(id+"F28.imprint","IMPRINT",EDGE,{"disambiguationData":[TD([[subQ3,-1.0]])],"derivedFrom":subQ0}),1.0]])]});}
            extrude(context, id + "F33", {"entities" : qUnion([Q0, Q1, Q2, Q3, Q4, Q5, Q6, Q7, Q8, Q9]), "operationType" : NewBodyOperationType.REMOVE, "oppositeDirection" : true, "depth" : 25 * mm, "offsetDistance" : 25 * mm, "hasDraft" : true, "draftAngle" : 45 * degree, "draftPullDirection" : true});
        }
        {
            var Q0;
            Q0=makeQuery(id+"F18.opRevolve","SWEPT_FACE",FACE,{"disambiguationData":[OSD([sQuery(id+"F17.wireOp",EDGE,"E13")])]});
            var sketch = newSketch(context, id + "F34", { "sketchPlane" : qUnion([Q0])});
            skLineSegment(sketch, "E146", {"start": v(-0.01, 0.04) * mm, "end": v(32.49, 0.04) * mm});
            skLineSegment(sketch, "E147.1.0", {"start": v(-0.01, 0.04) * mm, "end": v(19.02, 6.23) * mm});
            skLineSegment(sketch, "E147.2.0", {"start": v(-0.01, 0.04) * mm, "end": v(16.18, 11.8) * mm});
            skLineSegment(sketch, "E147.3.0", {"start": v(-0.01, 0.04) * mm, "end": v(19.09, 26.33) * mm});
            skLineSegment(sketch, "E147.4.0", {"start": v(-0.01, 0.04) * mm, "end": v(10.03, 30.95) * mm});
            skLineSegment(sketch, "E147.5.0", {"start": v(-0.01, 0.04) * mm, "end": v(-0.01, 32.54) * mm});
            skLineSegment(sketch, "E147.6.0", {"start": v(-0.01, 0.04) * mm, "end": v(-10.06, 30.95) * mm});
            skLineSegment(sketch, "E147.7.0", {"start": v(-0.01, 0.04) * mm, "end": v(-19.12, 26.33) * mm});
            skLineSegment(sketch, "E147.8.0", {"start": v(-0.01, 0.04) * mm, "end": v(-26.3, 19.14) * mm});
            skLineSegment(sketch, "E147.9.0", {"start": v(-0.01, 0.04) * mm, "end": v(-19.05, 6.23) * mm});
            skLineSegment(sketch, "E147.10.0", {"start": v(-0.01, 0.04) * mm, "end": v(-32.51, 0.04) * mm});
            skLineSegment(sketch, "E147.11.0", {"start": v(-0.01, 0.04) * mm, "end": v(-30.92, -10) * mm});
            skLineSegment(sketch, "E147.12.0", {"start": v(-0.01, 0.04) * mm, "end": v(-16.2, -11.72) * mm});
            skLineSegment(sketch, "E147.13.0", {"start": v(-0.01, 0.04) * mm, "end": v(-19.12, -26.25) * mm});
            skLineSegment(sketch, "E147.14.0", {"start": v(-0.01, 0.04) * mm, "end": v(-6.2, -19) * mm});
            skLineSegment(sketch, "E147.15.0", {"start": v(-0.01, 0.04) * mm, "end": v(-0.01, -19.97) * mm});
            skLineSegment(sketch, "E147.16.0", {"start": v(-0.01, 0.04) * mm, "end": v(6.17, -19) * mm});
            skLineSegment(sketch, "E147.17.0", {"start": v(-0.01, 0.04) * mm, "end": v(19.09, -26.25) * mm});
            skLineSegment(sketch, "E147.18.0", {"start": v(-0.01, 0.04) * mm, "end": v(16.18, -11.72) * mm});
            skLineSegment(sketch, "E147.19.0", {"start": v(-0.01, 0.04) * mm, "end": v(30.9, -10) * mm});
            skPoint(sketch, "E147.center", {"position": v(-0.01, 0.04) * mm});
            skCircle(sketch, "E148", {"center": v(-0.01, 0.04) * mm, "radius": 32.5 * mm});
            skArc(sketch, "E149", {"start": v(-16.2, 11.8) * mm, "mid": v(-19.05, 6.23) * mm, "end": v(-20.03, 0.04) * mm});
            skArc(sketch, "E150", {"start": v(-11.78, 16.23) * mm, "mid": v(-14.17, 14.2) * mm, "end": v(-16.2, 11.8) * mm});
            skArc(sketch, "E151", {"start": v(-6.2, 19.08) * mm, "mid": v(-9.1, 17.87) * mm, "end": v(-11.78, 16.23) * mm});
            skArc(sketch, "E152", {"start": v(-0.01, 20.06) * mm, "mid": v(-3.14, 19.81) * mm, "end": v(-6.2, 19.08) * mm});
            skArc(sketch, "E153", {"start": v(6.17, 19.08) * mm, "mid": v(3.12, 19.81) * mm, "end": v(-0.01, 20.06) * mm});
            skArc(sketch, "E154", {"start": v(11.75, 16.23) * mm, "mid": v(9.07, 17.87) * mm, "end": v(6.17, 19.08) * mm});
            skLineSegment(sketch, "E155", {"start": v(16.18, 11.8) * mm, "end": v(26.28, 19.14) * mm});
            skLineSegment(sketch, "E156", {"start": v(19.02, 6.23) * mm, "end": v(30.9, 10.08) * mm});
            skArc(sketch, "E157", {"start": v(20, 0.04) * mm, "mid": v(17.82, 9.13) * mm, "end": v(11.75, 16.23) * mm});
            skArc(sketch, "E158", {"start": v(19.02, -6.14) * mm, "mid": v(19.75, -3.09) * mm, "end": v(20, 0.04) * mm});
            skLineSegment(sketch, "E159", {"start": v(16.18, -11.72) * mm, "end": v(26.28, -19.06) * mm});
            skArc(sketch, "E160", {"start": v(11.75, -16.15) * mm, "mid": v(16.18, -11.72) * mm, "end": v(19.02, -6.14) * mm});
            skLineSegment(sketch, "E161", {"start": v(6.17, -19) * mm, "end": v(10.03, -30.87) * mm});
            skLineSegment(sketch, "E162", {"start": v(-0.01, -19.97) * mm, "end": v(-0.01, -32.46) * mm});
            skLineSegment(sketch, "E163", {"start": v(-6.2, -19) * mm, "end": v(-10.06, -30.87) * mm});
            skArc(sketch, "E164", {"start": v(-11.78, -16.15) * mm, "mid": v(-0.01, -19.97) * mm, "end": v(11.75, -16.15) * mm});
            skLineSegment(sketch, "E165", {"start": v(-16.2, -11.72) * mm, "end": v(-26.3, -19.06) * mm});
            skArc(sketch, "E166", {"start": v(-19.05, -6.14) * mm, "mid": v(-16.2, -11.72) * mm, "end": v(-11.78, -16.15) * mm});
            skArc(sketch, "E167", {"start": v(-20.03, 0.04) * mm, "mid": v(-19.78, -3.09) * mm, "end": v(-19.05, -6.14) * mm});
            skLineSegment(sketch, "E168", {"start": v(-19.05, 6.23) * mm, "end": v(-30.92, 10.08) * mm});
            skSolve(sketch);
        }
        {
            var Q0;
            {var subQ5=sQuery(id+"F34.wireOp",EDGE,"E165");Q0=makeQuery(id+"F34.imprint","IMPRINT",FACE,{"disambiguationData":[TD([[makeQuery(id+"F34.imprint","IMPRINT",EDGE,{"derivedFrom":subQ5}),-1.0]])]});}
            var Q1;
            {var subQ0=sQuery(id+"F34.wireOp",EDGE,"E149");var subQ1=sQuery(id+"F34.wireOp",EDGE,"E147.10.0");var subQ2=makeQuery(id+"F34.imprint","INTERSECT",VERTEX,{"derivedFrom":[subQ1,subQ0,sQuery(id+"F34.wireOp",EDGE,"E167")]});Q1=makeQuery(id+"F34.imprint","IMPRINT",FACE,{"disambiguationData":[TD([[makeQuery(id+"F34.imprint","IMPRINT",EDGE,{"disambiguationData":[TD([[subQ2,-1.0]])],"derivedFrom":subQ1}),-1.0]])]});}
            var Q2;
            {var subQ0=sQuery(id+"F34.wireOp",EDGE,"E150");Q2=makeQuery(id+"F34.imprint","IMPRINT",FACE,{"disambiguationData":[TD([[makeQuery(id+"F34.imprint","IMPRINT",EDGE,{"derivedFrom":subQ0}),-1.0]])]});}
            var Q3;
            {var subQ0=sQuery(id+"F34.wireOp",EDGE,"E152");Q3=makeQuery(id+"F34.imprint","IMPRINT",FACE,{"disambiguationData":[TD([[makeQuery(id+"F34.imprint","IMPRINT",EDGE,{"derivedFrom":subQ0}),-1.0]])]});}
            var Q4;
            {var subQ0=sQuery(id+"F34.wireOp",EDGE,"E154");Q4=makeQuery(id+"F34.imprint","IMPRINT",FACE,{"disambiguationData":[TD([[makeQuery(id+"F34.imprint","IMPRINT",EDGE,{"derivedFrom":subQ0}),-1.0]])]});}
            var Q5;
            {var subQ0=sQuery(id+"F34.wireOp",EDGE,"E157");var subQ1=sQuery(id+"F34.wireOp",EDGE,"E155");var subQ2=makeQuery(id+"F34.imprint","INTERSECT",VERTEX,{"derivedFrom":[sQuery(id+"F34.wireOp",EDGE,"E147.2.0"),subQ1,subQ0]});Q5=makeQuery(id+"F34.imprint","IMPRINT",FACE,{"disambiguationData":[TD([[makeQuery(id+"F34.imprint","IMPRINT",EDGE,{"disambiguationData":[TD([[subQ2,-1.0]])],"derivedFrom":subQ1}),-1.0]])]});}
            var Q6;
            {var subQ3=sQuery(id+"F34.wireOp",EDGE,"E158");Q6=makeQuery(id+"F34.imprint","IMPRINT",FACE,{"disambiguationData":[TD([[makeQuery(id+"F34.imprint","IMPRINT",EDGE,{"derivedFrom":subQ3}),-1.0]])]});}
            var Q7;
            {var subQ5=sQuery(id+"F34.wireOp",EDGE,"E159");Q7=makeQuery(id+"F34.imprint","IMPRINT",FACE,{"disambiguationData":[TD([[makeQuery(id+"F34.imprint","IMPRINT",EDGE,{"derivedFrom":subQ5}),-1.0]])]});}
            var Q8;
            {var subQ0=sQuery(id+"F34.wireOp",EDGE,"E161");Q8=makeQuery(id+"F34.imprint","IMPRINT",FACE,{"disambiguationData":[TD([[makeQuery(id+"F34.imprint","IMPRINT",EDGE,{"derivedFrom":subQ0}),-1.0]])]});}
            var Q9;
            {var subQ5=sQuery(id+"F34.wireOp",EDGE,"E163");Q9=makeQuery(id+"F34.imprint","IMPRINT",FACE,{"disambiguationData":[TD([[makeQuery(id+"F34.imprint","IMPRINT",EDGE,{"derivedFrom":subQ5}),-1.0]])]});}
            var Q10;
            {var subQ0=sQuery(id+"F34.wireOp",EDGE,"E158");var subQ1=sQuery(id+"F34.wireOp",EDGE,"E146");var subQ2=makeQuery(id+"F34.imprint","INTERSECT",VERTEX,{"derivedFrom":[subQ1,sQuery(id+"F34.wireOp",EDGE,"E157"),subQ0]});Q10=makeQuery(id+"F34.imprint","IMPRINT",FACE,{"disambiguationData":[TD([[makeQuery(id+"F34.imprint","IMPRINT",EDGE,{"disambiguationData":[TD([[subQ2,-1.0]])],"derivedFrom":subQ1}),-1.0]])]});}
            extrude(context, id + "F35", {"entities" : qUnion([Q0, Q1, Q2, Q3, Q4, Q5, Q6, Q7, Q8, Q9, Q10]), "operationType" : NewBodyOperationType.REMOVE, "oppositeDirection" : true, "depth" : 25 * mm, "offsetDistance" : 25 * mm, "hasDraft" : true, "draftAngle" : 45 * degree, "draftPullDirection" : true});
        }
        {
            var Q0;
            {var subQ0=sQuery(id+"F34.wireOp",EDGE,"E157");var subQ1=sQuery(id+"F34.wireOp",EDGE,"E146");var subQ2=makeQuery(id+"F34.imprint","INTERSECT",VERTEX,{"derivedFrom":[subQ1,subQ0,sQuery(id+"F34.wireOp",EDGE,"E158")]});Q0=makeQuery(id+"F34.imprint","IMPRINT",FACE,{"disambiguationData":[TD([[makeQuery(id+"F34.imprint","IMPRINT",EDGE,{"disambiguationData":[TD([[subQ2,-1.0]])],"derivedFrom":subQ1}),1.0]])]});}
            var Q1;
            {var subQ0=sQuery(id+"F34.wireOp",EDGE,"E157");var subQ1=sQuery(id+"F34.wireOp",EDGE,"E147.3.0");var subQ2=makeQuery(id+"F34.imprint","INTERSECT",VERTEX,{"derivedFrom":[subQ1,sQuery(id+"F34.wireOp",EDGE,"E154"),subQ0]});Q1=makeQuery(id+"F34.imprint","IMPRINT",FACE,{"disambiguationData":[TD([[makeQuery(id+"F34.imprint","IMPRINT",EDGE,{"disambiguationData":[TD([[subQ2,-1.0]])],"derivedFrom":subQ1}),-1.0]])]});}
            var Q2;
            {var subQ0=sQuery(id+"F34.wireOp",EDGE,"E153");Q2=makeQuery(id+"F34.imprint","IMPRINT",FACE,{"disambiguationData":[TD([[makeQuery(id+"F34.imprint","IMPRINT",EDGE,{"derivedFrom":subQ0}),-1.0]])]});}
            var Q3;
            {var subQ0=sQuery(id+"F34.wireOp",EDGE,"E147.19.0");var subQ1=sQuery(id+"F17.wireOp",EDGE,"E13");var subQ2=makeQuery(id+"F18.opRevolve","SWEPT_EDGE",EDGE,{"disambiguationData":[OSD([subQ1,sQuery(id+"F17.wireOp",EDGE,"E14")])]});var subQ3=makeQuery(id+"F34.imprint","INTERSECT",VERTEX,{"derivedFrom":[subQ2,subQ0]});Q3=makeQuery(id+"F34.imprint","IMPRINT",FACE,{"disambiguationData":[TD([[makeQuery(id+"F34.imprint","IMPRINT",EDGE,{"disambiguationData":[TD([[subQ3,-1.0]])],"derivedFrom":subQ0}),-1.0]])]});}
            var Q4;
            {var subQ0=sQuery(id+"F34.wireOp",EDGE,"E147.17.0");var subQ1=sQuery(id+"F17.wireOp",EDGE,"E13");var subQ2=makeQuery(id+"F18.opRevolve","SWEPT_EDGE",EDGE,{"disambiguationData":[OSD([subQ1,sQuery(id+"F17.wireOp",EDGE,"E14")])]});var subQ3=makeQuery(id+"F34.imprint","INTERSECT",VERTEX,{"derivedFrom":[subQ2,subQ0]});Q4=makeQuery(id+"F34.imprint","IMPRINT",FACE,{"disambiguationData":[TD([[makeQuery(id+"F34.imprint","IMPRINT",EDGE,{"disambiguationData":[TD([[subQ3,-1.0]])],"derivedFrom":subQ0}),-1.0]])]});}
            var Q5;
            {var subQ0=sQuery(id+"F34.wireOp",EDGE,"E162");var subQ1=sQuery(id+"F17.wireOp",EDGE,"E13");var subQ2=makeQuery(id+"F18.opRevolve","SWEPT_EDGE",EDGE,{"disambiguationData":[OSD([subQ1,sQuery(id+"F17.wireOp",EDGE,"E14")])]});var subQ3=makeQuery(id+"F34.imprint","INTERSECT",VERTEX,{"derivedFrom":[subQ2,subQ0]});Q5=makeQuery(id+"F34.imprint","IMPRINT",FACE,{"disambiguationData":[TD([[makeQuery(id+"F34.imprint","IMPRINT",EDGE,{"disambiguationData":[TD([[subQ3,-1.0]])],"derivedFrom":subQ0}),-1.0]])]});}
            var Q6;
            {var subQ0=sQuery(id+"F34.wireOp",EDGE,"E147.13.0");var subQ1=sQuery(id+"F17.wireOp",EDGE,"E13");var subQ6=makeQuery(id+"F18.opRevolve","SWEPT_EDGE",EDGE,{"disambiguationData":[OSD([subQ1,sQuery(id+"F17.wireOp",EDGE,"E14")])]});var subQ7=makeQuery(id+"F34.imprint","INTERSECT",VERTEX,{"derivedFrom":[subQ6,subQ0]});Q6=makeQuery(id+"F34.imprint","IMPRINT",FACE,{"disambiguationData":[TD([[makeQuery(id+"F34.imprint","IMPRINT",EDGE,{"disambiguationData":[TD([[subQ7,-1.0]])],"derivedFrom":subQ0}),-1.0]])]});}
            var Q7;
            {var subQ0=sQuery(id+"F34.wireOp",EDGE,"E167");Q7=makeQuery(id+"F34.imprint","IMPRINT",FACE,{"disambiguationData":[TD([[makeQuery(id+"F34.imprint","IMPRINT",EDGE,{"derivedFrom":subQ0}),-1.0]])]});}
            var Q8;
            {var subQ0=sQuery(id+"F34.wireOp",EDGE,"E149");var subQ1=sQuery(id+"F34.wireOp",EDGE,"E147.8.0");var subQ2=makeQuery(id+"F34.imprint","INTERSECT",VERTEX,{"derivedFrom":[subQ1,subQ0,sQuery(id+"F34.wireOp",EDGE,"E150")]});Q8=makeQuery(id+"F34.imprint","IMPRINT",FACE,{"disambiguationData":[TD([[makeQuery(id+"F34.imprint","IMPRINT",EDGE,{"disambiguationData":[TD([[subQ2,-1.0]])],"derivedFrom":subQ1}),1.0]])]});}
            var Q9;
            {var subQ0=sQuery(id+"F34.wireOp",EDGE,"E151");Q9=makeQuery(id+"F34.imprint","IMPRINT",FACE,{"disambiguationData":[TD([[makeQuery(id+"F34.imprint","IMPRINT",EDGE,{"derivedFrom":subQ0}),-1.0]])]});}
            extrude(context, id + "F36", {"entities" : qUnion([Q0, Q1, Q2, Q3, Q4, Q5, Q6, Q7, Q8, Q9]), "operationType" : NewBodyOperationType.REMOVE, "oppositeDirection" : true, "depth" : 5 * mm, "offsetDistance" : 25 * mm, "hasDraft" : true, "draftAngle" : 45 * degree, "draftPullDirection" : true});
        }
        {
            var Q0;
            Q0=makeQuery(id+"F20.opRevolve","SWEPT_FACE",FACE,{"disambiguationData":[OSD([sQuery(id+"F19.wireOp",EDGE,"E28")])]});
            var sketch = newSketch(context, id + "F37", { "sketchPlane" : qUnion([Q0])});
            skLineSegment(sketch, "E169", {"start": v(-0.01, 0.04) * mm, "end": v(32.49, 0.04) * mm});
            skLineSegment(sketch, "E170.1.0", {"start": v(-0.01, 0.04) * mm, "end": v(19.02, 6.23) * mm});
            skLineSegment(sketch, "E170.2.0", {"start": v(-0.01, 0.04) * mm, "end": v(16.18, 11.8) * mm});
            skLineSegment(sketch, "E170.3.0", {"start": v(-0.01, 0.04) * mm, "end": v(19.09, 26.33) * mm});
            skLineSegment(sketch, "E170.4.0", {"start": v(-0.01, 0.04) * mm, "end": v(10.03, 30.95) * mm});
            skLineSegment(sketch, "E170.5.0", {"start": v(-0.01, 0.04) * mm, "end": v(-0.01, 32.54) * mm});
            skLineSegment(sketch, "E170.6.0", {"start": v(-0.01, 0.04) * mm, "end": v(-10.06, 30.95) * mm});
            skLineSegment(sketch, "E170.7.0", {"start": v(-0.01, 0.04) * mm, "end": v(-19.12, 26.33) * mm});
            skLineSegment(sketch, "E170.8.0", {"start": v(-0.01, 0.04) * mm, "end": v(-26.3, 19.14) * mm});
            skLineSegment(sketch, "E170.9.0", {"start": v(-0.01, 0.04) * mm, "end": v(-19.05, 6.23) * mm});
            skLineSegment(sketch, "E170.10.0", {"start": v(-0.01, 0.04) * mm, "end": v(-32.51, 0.04) * mm});
            skLineSegment(sketch, "E170.11.0", {"start": v(-0.01, 0.04) * mm, "end": v(-30.92, -10) * mm});
            skLineSegment(sketch, "E170.12.0", {"start": v(-0.01, 0.04) * mm, "end": v(-16.2, -11.72) * mm});
            skLineSegment(sketch, "E170.13.0", {"start": v(-0.01, 0.04) * mm, "end": v(-19.12, -26.25) * mm});
            skLineSegment(sketch, "E170.14.0", {"start": v(-0.01, 0.04) * mm, "end": v(-6.2, -19) * mm});
            skLineSegment(sketch, "E170.15.0", {"start": v(-0.01, 0.04) * mm, "end": v(-0.01, -19.97) * mm});
            skLineSegment(sketch, "E170.16.0", {"start": v(-0.01, 0.04) * mm, "end": v(6.17, -19) * mm});
            skLineSegment(sketch, "E170.17.0", {"start": v(-0.01, 0.04) * mm, "end": v(19.09, -26.25) * mm});
            skLineSegment(sketch, "E170.18.0", {"start": v(-0.01, 0.04) * mm, "end": v(16.18, -11.72) * mm});
            skLineSegment(sketch, "E170.19.0", {"start": v(-0.01, 0.04) * mm, "end": v(30.9, -10) * mm});
            skPoint(sketch, "E170.center", {"position": v(-0.01, 0.04) * mm});
            skCircle(sketch, "E171", {"center": v(-0.01, 0.04) * mm, "radius": 32.5 * mm});
            skArc(sketch, "E172", {"start": v(-16.2, 11.8) * mm, "mid": v(-19.05, 6.23) * mm, "end": v(-20.03, 0.04) * mm});
            skArc(sketch, "E173", {"start": v(-11.78, 16.23) * mm, "mid": v(-14.17, 14.2) * mm, "end": v(-16.2, 11.8) * mm});
            skArc(sketch, "E174", {"start": v(-6.2, 19.08) * mm, "mid": v(-9.1, 17.87) * mm, "end": v(-11.78, 16.23) * mm});
            skArc(sketch, "E175", {"start": v(-0.01, 20.06) * mm, "mid": v(-3.14, 19.81) * mm, "end": v(-6.2, 19.08) * mm});
            skArc(sketch, "E176", {"start": v(6.17, 19.08) * mm, "mid": v(3.12, 19.81) * mm, "end": v(-0.01, 20.06) * mm});
            skArc(sketch, "E177", {"start": v(11.75, 16.23) * mm, "mid": v(9.07, 17.87) * mm, "end": v(6.17, 19.08) * mm});
            skLineSegment(sketch, "E178", {"start": v(16.18, 11.8) * mm, "end": v(26.28, 19.14) * mm});
            skLineSegment(sketch, "E179", {"start": v(19.02, 6.23) * mm, "end": v(30.9, 10.08) * mm});
            skArc(sketch, "E180", {"start": v(20, 0.04) * mm, "mid": v(17.82, 9.13) * mm, "end": v(11.75, 16.23) * mm});
            skArc(sketch, "E181", {"start": v(19.02, -6.14) * mm, "mid": v(19.75, -3.09) * mm, "end": v(20, 0.04) * mm});
            skLineSegment(sketch, "E182", {"start": v(16.18, -11.72) * mm, "end": v(26.28, -19.06) * mm});
            skArc(sketch, "E183", {"start": v(11.75, -16.15) * mm, "mid": v(16.18, -11.72) * mm, "end": v(19.02, -6.14) * mm});
            skLineSegment(sketch, "E184", {"start": v(6.17, -19) * mm, "end": v(10.03, -30.87) * mm});
            skLineSegment(sketch, "E185", {"start": v(-0.01, -19.97) * mm, "end": v(-0.01, -32.46) * mm});
            skLineSegment(sketch, "E186", {"start": v(-6.2, -19) * mm, "end": v(-10.06, -30.87) * mm});
            skArc(sketch, "E187", {"start": v(-11.78, -16.15) * mm, "mid": v(-0.01, -19.97) * mm, "end": v(11.75, -16.15) * mm});
            skLineSegment(sketch, "E188", {"start": v(-16.2, -11.72) * mm, "end": v(-26.3, -19.06) * mm});
            skArc(sketch, "E189", {"start": v(-19.05, -6.14) * mm, "mid": v(-16.2, -11.72) * mm, "end": v(-11.78, -16.15) * mm});
            skArc(sketch, "E190", {"start": v(-20.03, 0.04) * mm, "mid": v(-19.78, -3.09) * mm, "end": v(-19.05, -6.14) * mm});
            skLineSegment(sketch, "E191", {"start": v(-19.05, 6.23) * mm, "end": v(-30.92, 10.08) * mm});
            skSolve(sketch);
        }
        {
            var Q0;
            {var subQ0=sQuery(id+"F37.wireOp",EDGE,"E169");var subQ1=sQuery(id+"F19.wireOp",EDGE,"E28");var subQ2=makeQuery(id+"F20.opRevolve","SWEPT_EDGE",EDGE,{"disambiguationData":[OSD([subQ1,sQuery(id+"F19.wireOp",EDGE,"E35")])]});var subQ3=makeQuery(id+"F37.imprint","INTERSECT",VERTEX,{"derivedFrom":[subQ2,subQ0]});Q0=makeQuery(id+"F37.imprint","IMPRINT",FACE,{"disambiguationData":[TD([[makeQuery(id+"F37.imprint","IMPRINT",EDGE,{"disambiguationData":[TD([[subQ3,-1.0]])],"derivedFrom":subQ0}),1.0]])]});}
            var Q1;
            {var subQ0=sQuery(id+"F37.wireOp",EDGE,"E170.2.0");var subQ1=sQuery(id+"F19.wireOp",EDGE,"E28");var subQ2=makeQuery(id+"F20.opRevolve","SWEPT_EDGE",EDGE,{"disambiguationData":[OSD([subQ1,sQuery(id+"F19.wireOp",EDGE,"E35")])]});var subQ3=makeQuery(id+"F37.imprint","INTERSECT",VERTEX,{"derivedFrom":[subQ2,subQ0]});Q1=makeQuery(id+"F37.imprint","IMPRINT",FACE,{"disambiguationData":[TD([[makeQuery(id+"F37.imprint","IMPRINT",EDGE,{"disambiguationData":[TD([[subQ3,-1.0]])],"derivedFrom":subQ0}),1.0]])]});}
            var Q2;
            {var subQ0=sQuery(id+"F37.wireOp",EDGE,"E170.4.0");var subQ1=sQuery(id+"F19.wireOp",EDGE,"E28");var subQ2=makeQuery(id+"F20.opRevolve","SWEPT_EDGE",EDGE,{"disambiguationData":[OSD([subQ1,sQuery(id+"F19.wireOp",EDGE,"E35")])]});var subQ3=makeQuery(id+"F37.imprint","INTERSECT",VERTEX,{"derivedFrom":[subQ2,subQ0]});Q2=makeQuery(id+"F37.imprint","IMPRINT",FACE,{"disambiguationData":[TD([[makeQuery(id+"F37.imprint","IMPRINT",EDGE,{"disambiguationData":[TD([[subQ3,-1.0]])],"derivedFrom":subQ0}),1.0]])]});}
            var Q3;
            {var subQ0=sQuery(id+"F37.wireOp",EDGE,"E170.6.0");var subQ1=sQuery(id+"F19.wireOp",EDGE,"E28");var subQ2=makeQuery(id+"F20.opRevolve","SWEPT_EDGE",EDGE,{"disambiguationData":[OSD([subQ1,sQuery(id+"F19.wireOp",EDGE,"E35")])]});var subQ3=makeQuery(id+"F37.imprint","INTERSECT",VERTEX,{"derivedFrom":[subQ2,subQ0]});Q3=makeQuery(id+"F37.imprint","IMPRINT",FACE,{"disambiguationData":[TD([[makeQuery(id+"F37.imprint","IMPRINT",EDGE,{"disambiguationData":[TD([[subQ3,-1.0]])],"derivedFrom":subQ0}),1.0]])]});}
            var Q4;
            {var subQ0=sQuery(id+"F37.wireOp",EDGE,"E170.8.0");var subQ1=sQuery(id+"F19.wireOp",EDGE,"E28");var subQ2=makeQuery(id+"F20.opRevolve","SWEPT_EDGE",EDGE,{"disambiguationData":[OSD([subQ1,sQuery(id+"F19.wireOp",EDGE,"E35")])]});var subQ3=makeQuery(id+"F37.imprint","INTERSECT",VERTEX,{"derivedFrom":[subQ2,subQ0]});Q4=makeQuery(id+"F37.imprint","IMPRINT",FACE,{"disambiguationData":[TD([[makeQuery(id+"F37.imprint","IMPRINT",EDGE,{"disambiguationData":[TD([[subQ3,-1.0]])],"derivedFrom":subQ0}),1.0]])]});}
            var Q5;
            {var subQ0=sQuery(id+"F37.wireOp",EDGE,"E170.10.0");var subQ1=sQuery(id+"F19.wireOp",EDGE,"E28");var subQ2=makeQuery(id+"F20.opRevolve","SWEPT_EDGE",EDGE,{"disambiguationData":[OSD([subQ1,sQuery(id+"F19.wireOp",EDGE,"E35")])]});var subQ3=makeQuery(id+"F37.imprint","INTERSECT",VERTEX,{"derivedFrom":[subQ2,subQ0]});Q5=makeQuery(id+"F37.imprint","IMPRINT",FACE,{"disambiguationData":[TD([[makeQuery(id+"F37.imprint","IMPRINT",EDGE,{"disambiguationData":[TD([[subQ3,-1.0]])],"derivedFrom":subQ0}),1.0]])]});}
            var Q6;
            {var subQ0=sQuery(id+"F37.wireOp",EDGE,"E170.12.0");var subQ1=sQuery(id+"F19.wireOp",EDGE,"E28");var subQ2=makeQuery(id+"F20.opRevolve","SWEPT_EDGE",EDGE,{"disambiguationData":[OSD([subQ1,sQuery(id+"F19.wireOp",EDGE,"E35")])]});var subQ3=makeQuery(id+"F37.imprint","INTERSECT",VERTEX,{"derivedFrom":[subQ2,subQ0]});Q6=makeQuery(id+"F37.imprint","IMPRINT",FACE,{"disambiguationData":[TD([[makeQuery(id+"F37.imprint","IMPRINT",EDGE,{"disambiguationData":[TD([[subQ3,-1.0]])],"derivedFrom":subQ0}),1.0]])]});}
            var Q7;
            {var subQ0=sQuery(id+"F37.wireOp",EDGE,"E170.14.0");var subQ1=sQuery(id+"F19.wireOp",EDGE,"E28");var subQ2=makeQuery(id+"F20.opRevolve","SWEPT_EDGE",EDGE,{"disambiguationData":[OSD([subQ1,sQuery(id+"F19.wireOp",EDGE,"E35")])]});var subQ3=makeQuery(id+"F37.imprint","INTERSECT",VERTEX,{"derivedFrom":[subQ2,subQ0]});Q7=makeQuery(id+"F37.imprint","IMPRINT",FACE,{"disambiguationData":[TD([[makeQuery(id+"F37.imprint","IMPRINT",EDGE,{"disambiguationData":[TD([[subQ3,-1.0]])],"derivedFrom":subQ0}),1.0]])]});}
            var Q8;
            {var subQ0=sQuery(id+"F37.wireOp",EDGE,"E170.16.0");var subQ1=sQuery(id+"F19.wireOp",EDGE,"E28");var subQ2=makeQuery(id+"F20.opRevolve","SWEPT_EDGE",EDGE,{"disambiguationData":[OSD([subQ1,sQuery(id+"F19.wireOp",EDGE,"E35")])]});var subQ3=makeQuery(id+"F37.imprint","INTERSECT",VERTEX,{"derivedFrom":[subQ2,subQ0]});Q8=makeQuery(id+"F37.imprint","IMPRINT",FACE,{"disambiguationData":[TD([[makeQuery(id+"F37.imprint","IMPRINT",EDGE,{"disambiguationData":[TD([[subQ3,-1.0]])],"derivedFrom":subQ0}),1.0]])]});}
            var Q9;
            {var subQ0=sQuery(id+"F37.wireOp",EDGE,"E170.18.0");var subQ1=sQuery(id+"F19.wireOp",EDGE,"E28");var subQ2=makeQuery(id+"F20.opRevolve","SWEPT_EDGE",EDGE,{"disambiguationData":[OSD([subQ1,sQuery(id+"F19.wireOp",EDGE,"E35")])]});var subQ3=makeQuery(id+"F37.imprint","INTERSECT",VERTEX,{"derivedFrom":[subQ2,subQ0]});Q9=makeQuery(id+"F37.imprint","IMPRINT",FACE,{"disambiguationData":[TD([[makeQuery(id+"F37.imprint","IMPRINT",EDGE,{"disambiguationData":[TD([[subQ3,-1.0]])],"derivedFrom":subQ0}),1.0]])]});}
            extrude(context, id + "F38", {"entities" : qUnion([Q0, Q1, Q2, Q3, Q4, Q5, Q6, Q7, Q8, Q9]), "operationType" : NewBodyOperationType.REMOVE, "oppositeDirection" : true, "depth" : 5 * mm, "offsetDistance" : 25 * mm, "hasDraft" : true, "draftAngle" : 45 * degree, "draftPullDirection" : true});
        }
        {
            var Q0;
            {var subQ0=sQuery(id+"F37.wireOp",EDGE,"E170.11.0");var subQ1=sQuery(id+"F19.wireOp",EDGE,"E28");var subQ2=makeQuery(id+"F20.opRevolve","SWEPT_EDGE",EDGE,{"disambiguationData":[OSD([subQ1,sQuery(id+"F19.wireOp",EDGE,"E35")])]});var subQ3=makeQuery(id+"F37.imprint","INTERSECT",VERTEX,{"derivedFrom":[subQ2,subQ0]});Q0=makeQuery(id+"F37.imprint","IMPRINT",FACE,{"disambiguationData":[TD([[makeQuery(id+"F37.imprint","IMPRINT",EDGE,{"disambiguationData":[TD([[subQ3,-1.0]])],"derivedFrom":subQ0}),1.0]])]});}
            var Q1;
            {var subQ0=sQuery(id+"F37.wireOp",EDGE,"E170.9.0");var subQ1=sQuery(id+"F19.wireOp",EDGE,"E28");var subQ2=makeQuery(id+"F20.opRevolve","SWEPT_EDGE",EDGE,{"disambiguationData":[OSD([subQ1,sQuery(id+"F19.wireOp",EDGE,"E35")])]});var subQ3=makeQuery(id+"F37.imprint","INTERSECT",VERTEX,{"derivedFrom":[subQ2,subQ0]});Q1=makeQuery(id+"F37.imprint","IMPRINT",FACE,{"disambiguationData":[TD([[makeQuery(id+"F37.imprint","IMPRINT",EDGE,{"disambiguationData":[TD([[subQ3,-1.0]])],"derivedFrom":subQ0}),1.0]])]});}
            var Q2;
            {var subQ0=sQuery(id+"F37.wireOp",EDGE,"E170.7.0");var subQ1=sQuery(id+"F19.wireOp",EDGE,"E28");var subQ2=makeQuery(id+"F20.opRevolve","SWEPT_EDGE",EDGE,{"disambiguationData":[OSD([subQ1,sQuery(id+"F19.wireOp",EDGE,"E35")])]});var subQ3=makeQuery(id+"F37.imprint","INTERSECT",VERTEX,{"derivedFrom":[subQ2,subQ0]});Q2=makeQuery(id+"F37.imprint","IMPRINT",FACE,{"disambiguationData":[TD([[makeQuery(id+"F37.imprint","IMPRINT",EDGE,{"disambiguationData":[TD([[subQ3,-1.0]])],"derivedFrom":subQ0}),1.0]])]});}
            var Q3;
            {var subQ0=sQuery(id+"F37.wireOp",EDGE,"E170.5.0");var subQ1=sQuery(id+"F19.wireOp",EDGE,"E28");var subQ2=makeQuery(id+"F20.opRevolve","SWEPT_EDGE",EDGE,{"disambiguationData":[OSD([subQ1,sQuery(id+"F19.wireOp",EDGE,"E35")])]});var subQ3=makeQuery(id+"F37.imprint","INTERSECT",VERTEX,{"derivedFrom":[subQ2,subQ0]});Q3=makeQuery(id+"F37.imprint","IMPRINT",FACE,{"disambiguationData":[TD([[makeQuery(id+"F37.imprint","IMPRINT",EDGE,{"disambiguationData":[TD([[subQ3,-1.0]])],"derivedFrom":subQ0}),1.0]])]});}
            var Q4;
            {var subQ0=sQuery(id+"F37.wireOp",EDGE,"E170.3.0");var subQ1=sQuery(id+"F19.wireOp",EDGE,"E28");var subQ2=makeQuery(id+"F20.opRevolve","SWEPT_EDGE",EDGE,{"disambiguationData":[OSD([subQ1,sQuery(id+"F19.wireOp",EDGE,"E35")])]});var subQ3=makeQuery(id+"F37.imprint","INTERSECT",VERTEX,{"derivedFrom":[subQ2,subQ0]});Q4=makeQuery(id+"F37.imprint","IMPRINT",FACE,{"disambiguationData":[TD([[makeQuery(id+"F37.imprint","IMPRINT",EDGE,{"disambiguationData":[TD([[subQ3,-1.0]])],"derivedFrom":subQ0}),1.0]])]});}
            var Q5;
            {var subQ0=sQuery(id+"F37.wireOp",EDGE,"E170.1.0");var subQ1=sQuery(id+"F19.wireOp",EDGE,"E28");var subQ2=makeQuery(id+"F20.opRevolve","SWEPT_EDGE",EDGE,{"disambiguationData":[OSD([subQ1,sQuery(id+"F19.wireOp",EDGE,"E35")])]});var subQ3=makeQuery(id+"F37.imprint","INTERSECT",VERTEX,{"derivedFrom":[subQ2,subQ0]});Q5=makeQuery(id+"F37.imprint","IMPRINT",FACE,{"disambiguationData":[TD([[makeQuery(id+"F37.imprint","IMPRINT",EDGE,{"disambiguationData":[TD([[subQ3,-1.0]])],"derivedFrom":subQ0}),1.0]])]});}
            var Q6;
            {var subQ0=sQuery(id+"F37.wireOp",EDGE,"E169");var subQ1=sQuery(id+"F19.wireOp",EDGE,"E28");var subQ2=makeQuery(id+"F20.opRevolve","SWEPT_EDGE",EDGE,{"disambiguationData":[OSD([subQ1,sQuery(id+"F19.wireOp",EDGE,"E35")])]});var subQ3=makeQuery(id+"F37.imprint","INTERSECT",VERTEX,{"derivedFrom":[subQ2,subQ0]});Q6=makeQuery(id+"F37.imprint","IMPRINT",FACE,{"disambiguationData":[TD([[makeQuery(id+"F37.imprint","IMPRINT",EDGE,{"disambiguationData":[TD([[subQ3,-1.0]])],"derivedFrom":subQ0}),-1.0]])]});}
            var Q7;
            {var subQ0=sQuery(id+"F37.wireOp",EDGE,"E170.17.0");var subQ1=sQuery(id+"F19.wireOp",EDGE,"E28");var subQ2=makeQuery(id+"F20.opRevolve","SWEPT_EDGE",EDGE,{"disambiguationData":[OSD([subQ1,sQuery(id+"F19.wireOp",EDGE,"E35")])]});var subQ3=makeQuery(id+"F37.imprint","INTERSECT",VERTEX,{"derivedFrom":[subQ2,subQ0]});Q7=makeQuery(id+"F37.imprint","IMPRINT",FACE,{"disambiguationData":[TD([[makeQuery(id+"F37.imprint","IMPRINT",EDGE,{"disambiguationData":[TD([[subQ3,-1.0]])],"derivedFrom":subQ0}),1.0]])]});}
            var Q8;
            {var subQ0=sQuery(id+"F37.wireOp",EDGE,"E170.15.0");var subQ1=sQuery(id+"F19.wireOp",EDGE,"E28");var subQ2=makeQuery(id+"F20.opRevolve","SWEPT_EDGE",EDGE,{"disambiguationData":[OSD([subQ1,sQuery(id+"F19.wireOp",EDGE,"E35")])]});var subQ3=makeQuery(id+"F37.imprint","INTERSECT",VERTEX,{"derivedFrom":[subQ2,subQ0]});Q8=makeQuery(id+"F37.imprint","IMPRINT",FACE,{"disambiguationData":[TD([[makeQuery(id+"F37.imprint","IMPRINT",EDGE,{"disambiguationData":[TD([[subQ3,-1.0]])],"derivedFrom":subQ0}),1.0]])]});}
            var Q9;
            {var subQ0=sQuery(id+"F37.wireOp",EDGE,"E170.13.0");var subQ1=sQuery(id+"F19.wireOp",EDGE,"E28");var subQ2=makeQuery(id+"F20.opRevolve","SWEPT_EDGE",EDGE,{"disambiguationData":[OSD([subQ1,sQuery(id+"F19.wireOp",EDGE,"E35")])]});var subQ3=makeQuery(id+"F37.imprint","INTERSECT",VERTEX,{"derivedFrom":[subQ2,subQ0]});Q9=makeQuery(id+"F37.imprint","IMPRINT",FACE,{"disambiguationData":[TD([[makeQuery(id+"F37.imprint","IMPRINT",EDGE,{"disambiguationData":[TD([[subQ3,-1.0]])],"derivedFrom":subQ0}),1.0]])]});}
            extrude(context, id + "F39", {"entities" : qUnion([Q0, Q1, Q2, Q3, Q4, Q5, Q6, Q7, Q8, Q9]), "operationType" : NewBodyOperationType.REMOVE, "oppositeDirection" : true, "depth" : 5 * mm, "offsetDistance" : 25 * mm, "hasDraft" : true, "draftAngle" : 45 * degree, "draftPullDirection" : true});
        }
        {
            var Q0;
            Q0=makeQuery(id+"F20.opRevolve","SWEPT_FACE",FACE,{"disambiguationData":[OSD([sQuery(id+"F19.wireOp",EDGE,"E30")])]});
            var sketch = newSketch(context, id + "F40", { "sketchPlane" : qUnion([Q0])});
            skLineSegment(sketch, "E192", {"start": v(-0.01, 0.04) * mm, "end": v(32.49, 0.04) * mm});
            skLineSegment(sketch, "E193.1.0", {"start": v(-0.01, 0.04) * mm, "end": v(19.02, 6.23) * mm});
            skLineSegment(sketch, "E193.2.0", {"start": v(-0.01, 0.04) * mm, "end": v(16.18, 11.8) * mm});
            skLineSegment(sketch, "E193.3.0", {"start": v(-0.01, 0.04) * mm, "end": v(19.09, 26.33) * mm});
            skLineSegment(sketch, "E193.4.0", {"start": v(-0.01, 0.04) * mm, "end": v(10.03, 30.95) * mm});
            skLineSegment(sketch, "E193.5.0", {"start": v(-0.01, 0.04) * mm, "end": v(-0.01, 32.54) * mm});
            skLineSegment(sketch, "E193.6.0", {"start": v(-0.01, 0.04) * mm, "end": v(-10.06, 30.95) * mm});
            skLineSegment(sketch, "E193.7.0", {"start": v(-0.01, 0.04) * mm, "end": v(-19.12, 26.33) * mm});
            skLineSegment(sketch, "E193.8.0", {"start": v(-0.01, 0.04) * mm, "end": v(-26.3, 19.14) * mm});
            skLineSegment(sketch, "E193.9.0", {"start": v(-0.01, 0.04) * mm, "end": v(-19.05, 6.23) * mm});
            skLineSegment(sketch, "E193.10.0", {"start": v(-0.01, 0.04) * mm, "end": v(-32.51, 0.04) * mm});
            skLineSegment(sketch, "E193.11.0", {"start": v(-0.01, 0.04) * mm, "end": v(-30.92, -10) * mm});
            skLineSegment(sketch, "E193.12.0", {"start": v(-0.01, 0.04) * mm, "end": v(-16.2, -11.72) * mm});
            skLineSegment(sketch, "E193.13.0", {"start": v(-0.01, 0.04) * mm, "end": v(-19.12, -26.25) * mm});
            skLineSegment(sketch, "E193.14.0", {"start": v(-0.01, 0.04) * mm, "end": v(-6.2, -19) * mm});
            skLineSegment(sketch, "E193.15.0", {"start": v(-0.01, 0.04) * mm, "end": v(-0.01, -19.97) * mm});
            skLineSegment(sketch, "E193.16.0", {"start": v(-0.01, 0.04) * mm, "end": v(6.17, -19) * mm});
            skLineSegment(sketch, "E193.17.0", {"start": v(-0.01, 0.04) * mm, "end": v(19.09, -26.25) * mm});
            skLineSegment(sketch, "E193.18.0", {"start": v(-0.01, 0.04) * mm, "end": v(16.18, -11.72) * mm});
            skLineSegment(sketch, "E193.19.0", {"start": v(-0.01, 0.04) * mm, "end": v(30.9, -10) * mm});
            skPoint(sketch, "E193.center", {"position": v(-0.01, 0.04) * mm});
            skCircle(sketch, "E194", {"center": v(-0.01, 0.04) * mm, "radius": 32.5 * mm});
            skArc(sketch, "E195", {"start": v(-16.2, 11.8) * mm, "mid": v(-19.05, 6.23) * mm, "end": v(-20.03, 0.04) * mm});
            skArc(sketch, "E196", {"start": v(-11.78, 16.23) * mm, "mid": v(-14.17, 14.2) * mm, "end": v(-16.2, 11.8) * mm});
            skArc(sketch, "E197", {"start": v(-6.2, 19.08) * mm, "mid": v(-9.1, 17.87) * mm, "end": v(-11.78, 16.23) * mm});
            skArc(sketch, "E198", {"start": v(-0.01, 20.06) * mm, "mid": v(-3.14, 19.81) * mm, "end": v(-6.2, 19.08) * mm});
            skArc(sketch, "E199", {"start": v(6.17, 19.08) * mm, "mid": v(3.12, 19.81) * mm, "end": v(-0.01, 20.06) * mm});
            skArc(sketch, "E200", {"start": v(11.75, 16.23) * mm, "mid": v(9.07, 17.87) * mm, "end": v(6.17, 19.08) * mm});
            skLineSegment(sketch, "E201", {"start": v(16.18, 11.8) * mm, "end": v(26.28, 19.14) * mm});
            skLineSegment(sketch, "E202", {"start": v(19.02, 6.23) * mm, "end": v(30.9, 10.08) * mm});
            skArc(sketch, "E203", {"start": v(20, 0.04) * mm, "mid": v(17.82, 9.13) * mm, "end": v(11.75, 16.23) * mm});
            skArc(sketch, "E204", {"start": v(19.02, -6.14) * mm, "mid": v(19.75, -3.09) * mm, "end": v(20, 0.04) * mm});
            skLineSegment(sketch, "E205", {"start": v(16.18, -11.72) * mm, "end": v(26.28, -19.06) * mm});
            skArc(sketch, "E206", {"start": v(11.75, -16.15) * mm, "mid": v(16.18, -11.72) * mm, "end": v(19.02, -6.14) * mm});
            skLineSegment(sketch, "E207", {"start": v(6.17, -19) * mm, "end": v(10.03, -30.87) * mm});
            skLineSegment(sketch, "E208", {"start": v(-0.01, -19.97) * mm, "end": v(-0.01, -32.46) * mm});
            skLineSegment(sketch, "E209", {"start": v(-6.2, -19) * mm, "end": v(-10.06, -30.87) * mm});
            skArc(sketch, "E210", {"start": v(-11.78, -16.15) * mm, "mid": v(-0.01, -19.97) * mm, "end": v(11.75, -16.15) * mm});
            skLineSegment(sketch, "E211", {"start": v(-16.2, -11.72) * mm, "end": v(-26.3, -19.06) * mm});
            skArc(sketch, "E212", {"start": v(-19.05, -6.14) * mm, "mid": v(-16.2, -11.72) * mm, "end": v(-11.78, -16.15) * mm});
            skArc(sketch, "E213", {"start": v(-20.03, 0.04) * mm, "mid": v(-19.78, -3.09) * mm, "end": v(-19.05, -6.14) * mm});
            skLineSegment(sketch, "E214", {"start": v(-19.05, 6.23) * mm, "end": v(-30.92, 10.08) * mm});
            skSolve(sketch);
        }
        {
            var Q0;
            {var subQ0=sQuery(id+"F40.wireOp",EDGE,"E193.12.0");var subQ1=sQuery(id+"F19.wireOp",EDGE,"E30");var subQ2=makeQuery(id+"F20.opRevolve","SWEPT_EDGE",EDGE,{"disambiguationData":[OSD([sQuery(id+"F19.wireOp",EDGE,"E29"),subQ1])]});var subQ3=makeQuery(id+"F40.imprint","INTERSECT",VERTEX,{"derivedFrom":[subQ2,subQ0]});Q0=makeQuery(id+"F40.imprint","IMPRINT",FACE,{"disambiguationData":[TD([[makeQuery(id+"F40.imprint","IMPRINT",EDGE,{"disambiguationData":[TD([[subQ3,-1.0]])],"derivedFrom":subQ0}),1.0]])]});}
            var Q1;
            {var subQ0=sQuery(id+"F40.wireOp",EDGE,"E193.14.0");var subQ1=sQuery(id+"F19.wireOp",EDGE,"E30");var subQ2=makeQuery(id+"F20.opRevolve","SWEPT_EDGE",EDGE,{"disambiguationData":[OSD([sQuery(id+"F19.wireOp",EDGE,"E29"),subQ1])]});var subQ3=makeQuery(id+"F40.imprint","INTERSECT",VERTEX,{"derivedFrom":[subQ2,subQ0]});Q1=makeQuery(id+"F40.imprint","IMPRINT",FACE,{"disambiguationData":[TD([[makeQuery(id+"F40.imprint","IMPRINT",EDGE,{"disambiguationData":[TD([[subQ3,-1.0]])],"derivedFrom":subQ0}),1.0]])]});}
            var Q2;
            {var subQ0=sQuery(id+"F40.wireOp",EDGE,"E193.16.0");var subQ1=sQuery(id+"F19.wireOp",EDGE,"E30");var subQ2=makeQuery(id+"F20.opRevolve","SWEPT_EDGE",EDGE,{"disambiguationData":[OSD([sQuery(id+"F19.wireOp",EDGE,"E29"),subQ1])]});var subQ3=makeQuery(id+"F40.imprint","INTERSECT",VERTEX,{"derivedFrom":[subQ2,subQ0]});Q2=makeQuery(id+"F40.imprint","IMPRINT",FACE,{"disambiguationData":[TD([[makeQuery(id+"F40.imprint","IMPRINT",EDGE,{"disambiguationData":[TD([[subQ3,-1.0]])],"derivedFrom":subQ0}),1.0]])]});}
            var Q3;
            {var subQ0=sQuery(id+"F40.wireOp",EDGE,"E193.18.0");var subQ1=sQuery(id+"F19.wireOp",EDGE,"E30");var subQ2=makeQuery(id+"F20.opRevolve","SWEPT_EDGE",EDGE,{"disambiguationData":[OSD([sQuery(id+"F19.wireOp",EDGE,"E29"),subQ1])]});var subQ3=makeQuery(id+"F40.imprint","INTERSECT",VERTEX,{"derivedFrom":[subQ2,subQ0]});Q3=makeQuery(id+"F40.imprint","IMPRINT",FACE,{"disambiguationData":[TD([[makeQuery(id+"F40.imprint","IMPRINT",EDGE,{"disambiguationData":[TD([[subQ3,-1.0]])],"derivedFrom":subQ0}),1.0]])]});}
            var Q4;
            {var subQ0=sQuery(id+"F40.wireOp",EDGE,"E192");var subQ1=sQuery(id+"F19.wireOp",EDGE,"E30");var subQ2=makeQuery(id+"F20.opRevolve","SWEPT_EDGE",EDGE,{"disambiguationData":[OSD([sQuery(id+"F19.wireOp",EDGE,"E29"),subQ1])]});var subQ3=makeQuery(id+"F40.imprint","INTERSECT",VERTEX,{"derivedFrom":[subQ2,subQ0]});Q4=makeQuery(id+"F40.imprint","IMPRINT",FACE,{"disambiguationData":[TD([[makeQuery(id+"F40.imprint","IMPRINT",EDGE,{"disambiguationData":[TD([[subQ3,-1.0]])],"derivedFrom":subQ0}),1.0]])]});}
            var Q5;
            {var subQ0=sQuery(id+"F40.wireOp",EDGE,"E193.2.0");var subQ1=sQuery(id+"F19.wireOp",EDGE,"E30");var subQ2=makeQuery(id+"F20.opRevolve","SWEPT_EDGE",EDGE,{"disambiguationData":[OSD([sQuery(id+"F19.wireOp",EDGE,"E29"),subQ1])]});var subQ3=makeQuery(id+"F40.imprint","INTERSECT",VERTEX,{"derivedFrom":[subQ2,subQ0]});Q5=makeQuery(id+"F40.imprint","IMPRINT",FACE,{"disambiguationData":[TD([[makeQuery(id+"F40.imprint","IMPRINT",EDGE,{"disambiguationData":[TD([[subQ3,-1.0]])],"derivedFrom":subQ0}),1.0]])]});}
            var Q6;
            {var subQ0=sQuery(id+"F40.wireOp",EDGE,"E193.4.0");var subQ1=sQuery(id+"F19.wireOp",EDGE,"E30");var subQ2=makeQuery(id+"F20.opRevolve","SWEPT_EDGE",EDGE,{"disambiguationData":[OSD([sQuery(id+"F19.wireOp",EDGE,"E29"),subQ1])]});var subQ3=makeQuery(id+"F40.imprint","INTERSECT",VERTEX,{"derivedFrom":[subQ2,subQ0]});Q6=makeQuery(id+"F40.imprint","IMPRINT",FACE,{"disambiguationData":[TD([[makeQuery(id+"F40.imprint","IMPRINT",EDGE,{"disambiguationData":[TD([[subQ3,-1.0]])],"derivedFrom":subQ0}),1.0]])]});}
            var Q7;
            {var subQ0=sQuery(id+"F40.wireOp",EDGE,"E193.6.0");var subQ1=sQuery(id+"F19.wireOp",EDGE,"E30");var subQ2=makeQuery(id+"F20.opRevolve","SWEPT_EDGE",EDGE,{"disambiguationData":[OSD([sQuery(id+"F19.wireOp",EDGE,"E29"),subQ1])]});var subQ3=makeQuery(id+"F40.imprint","INTERSECT",VERTEX,{"derivedFrom":[subQ2,subQ0]});Q7=makeQuery(id+"F40.imprint","IMPRINT",FACE,{"disambiguationData":[TD([[makeQuery(id+"F40.imprint","IMPRINT",EDGE,{"disambiguationData":[TD([[subQ3,-1.0]])],"derivedFrom":subQ0}),1.0]])]});}
            var Q8;
            {var subQ0=sQuery(id+"F40.wireOp",EDGE,"E193.8.0");var subQ1=sQuery(id+"F19.wireOp",EDGE,"E30");var subQ2=makeQuery(id+"F20.opRevolve","SWEPT_EDGE",EDGE,{"disambiguationData":[OSD([sQuery(id+"F19.wireOp",EDGE,"E29"),subQ1])]});var subQ3=makeQuery(id+"F40.imprint","INTERSECT",VERTEX,{"derivedFrom":[subQ2,subQ0]});Q8=makeQuery(id+"F40.imprint","IMPRINT",FACE,{"disambiguationData":[TD([[makeQuery(id+"F40.imprint","IMPRINT",EDGE,{"disambiguationData":[TD([[subQ3,-1.0]])],"derivedFrom":subQ0}),1.0]])]});}
            var Q9;
            {var subQ0=sQuery(id+"F40.wireOp",EDGE,"E193.10.0");var subQ1=sQuery(id+"F19.wireOp",EDGE,"E30");var subQ2=makeQuery(id+"F20.opRevolve","SWEPT_EDGE",EDGE,{"disambiguationData":[OSD([sQuery(id+"F19.wireOp",EDGE,"E29"),subQ1])]});var subQ3=makeQuery(id+"F40.imprint","INTERSECT",VERTEX,{"derivedFrom":[subQ2,subQ0]});Q9=makeQuery(id+"F40.imprint","IMPRINT",FACE,{"disambiguationData":[TD([[makeQuery(id+"F40.imprint","IMPRINT",EDGE,{"disambiguationData":[TD([[subQ3,-1.0]])],"derivedFrom":subQ0}),1.0]])]});}
            extrude(context, id + "F41", {"entities" : qUnion([Q0, Q1, Q2, Q3, Q4, Q5, Q6, Q7, Q8, Q9]), "operationType" : NewBodyOperationType.REMOVE, "oppositeDirection" : true, "depth" : 5 * mm, "offsetDistance" : 25 * mm, "hasDraft" : true, "draftAngle" : 45 * degree, "draftPullDirection" : true});
        }
        {
            var Q0;
            {var subQ0=sQuery(id+"F40.wireOp",EDGE,"E193.9.0");var subQ1=sQuery(id+"F19.wireOp",EDGE,"E30");var subQ2=makeQuery(id+"F20.opRevolve","SWEPT_EDGE",EDGE,{"disambiguationData":[OSD([sQuery(id+"F19.wireOp",EDGE,"E29"),subQ1])]});var subQ3=makeQuery(id+"F40.imprint","INTERSECT",VERTEX,{"derivedFrom":[subQ2,subQ0]});Q0=makeQuery(id+"F40.imprint","IMPRINT",FACE,{"disambiguationData":[TD([[makeQuery(id+"F40.imprint","IMPRINT",EDGE,{"disambiguationData":[TD([[subQ3,-1.0]])],"derivedFrom":subQ0}),1.0]])]});}
            var Q1;
            {var subQ0=sQuery(id+"F40.wireOp",EDGE,"E193.7.0");var subQ1=sQuery(id+"F19.wireOp",EDGE,"E30");var subQ2=makeQuery(id+"F20.opRevolve","SWEPT_EDGE",EDGE,{"disambiguationData":[OSD([sQuery(id+"F19.wireOp",EDGE,"E29"),subQ1])]});var subQ3=makeQuery(id+"F40.imprint","INTERSECT",VERTEX,{"derivedFrom":[subQ2,subQ0]});Q1=makeQuery(id+"F40.imprint","IMPRINT",FACE,{"disambiguationData":[TD([[makeQuery(id+"F40.imprint","IMPRINT",EDGE,{"disambiguationData":[TD([[subQ3,-1.0]])],"derivedFrom":subQ0}),1.0]])]});}
            var Q2;
            {var subQ0=sQuery(id+"F40.wireOp",EDGE,"E193.5.0");var subQ1=sQuery(id+"F19.wireOp",EDGE,"E30");var subQ2=makeQuery(id+"F20.opRevolve","SWEPT_EDGE",EDGE,{"disambiguationData":[OSD([sQuery(id+"F19.wireOp",EDGE,"E29"),subQ1])]});var subQ3=makeQuery(id+"F40.imprint","INTERSECT",VERTEX,{"derivedFrom":[subQ2,subQ0]});Q2=makeQuery(id+"F40.imprint","IMPRINT",FACE,{"disambiguationData":[TD([[makeQuery(id+"F40.imprint","IMPRINT",EDGE,{"disambiguationData":[TD([[subQ3,-1.0]])],"derivedFrom":subQ0}),1.0]])]});}
            var Q3;
            {var subQ0=sQuery(id+"F40.wireOp",EDGE,"E193.3.0");var subQ1=sQuery(id+"F19.wireOp",EDGE,"E30");var subQ2=makeQuery(id+"F20.opRevolve","SWEPT_EDGE",EDGE,{"disambiguationData":[OSD([sQuery(id+"F19.wireOp",EDGE,"E29"),subQ1])]});var subQ3=makeQuery(id+"F40.imprint","INTERSECT",VERTEX,{"derivedFrom":[subQ2,subQ0]});Q3=makeQuery(id+"F40.imprint","IMPRINT",FACE,{"disambiguationData":[TD([[makeQuery(id+"F40.imprint","IMPRINT",EDGE,{"disambiguationData":[TD([[subQ3,-1.0]])],"derivedFrom":subQ0}),1.0]])]});}
            var Q4;
            {var subQ0=sQuery(id+"F40.wireOp",EDGE,"E193.1.0");var subQ1=sQuery(id+"F19.wireOp",EDGE,"E30");var subQ2=makeQuery(id+"F20.opRevolve","SWEPT_EDGE",EDGE,{"disambiguationData":[OSD([sQuery(id+"F19.wireOp",EDGE,"E29"),subQ1])]});var subQ3=makeQuery(id+"F40.imprint","INTERSECT",VERTEX,{"derivedFrom":[subQ2,subQ0]});Q4=makeQuery(id+"F40.imprint","IMPRINT",FACE,{"disambiguationData":[TD([[makeQuery(id+"F40.imprint","IMPRINT",EDGE,{"disambiguationData":[TD([[subQ3,-1.0]])],"derivedFrom":subQ0}),1.0]])]});}
            var Q5;
            {var subQ0=sQuery(id+"F40.wireOp",EDGE,"E192");var subQ1=sQuery(id+"F19.wireOp",EDGE,"E30");var subQ2=makeQuery(id+"F20.opRevolve","SWEPT_EDGE",EDGE,{"disambiguationData":[OSD([sQuery(id+"F19.wireOp",EDGE,"E29"),subQ1])]});var subQ3=makeQuery(id+"F40.imprint","INTERSECT",VERTEX,{"derivedFrom":[subQ2,subQ0]});Q5=makeQuery(id+"F40.imprint","IMPRINT",FACE,{"disambiguationData":[TD([[makeQuery(id+"F40.imprint","IMPRINT",EDGE,{"disambiguationData":[TD([[subQ3,-1.0]])],"derivedFrom":subQ0}),-1.0]])]});}
            var Q6;
            {var subQ0=sQuery(id+"F40.wireOp",EDGE,"E193.17.0");var subQ1=sQuery(id+"F19.wireOp",EDGE,"E30");var subQ2=makeQuery(id+"F20.opRevolve","SWEPT_EDGE",EDGE,{"disambiguationData":[OSD([sQuery(id+"F19.wireOp",EDGE,"E29"),subQ1])]});var subQ3=makeQuery(id+"F40.imprint","INTERSECT",VERTEX,{"derivedFrom":[subQ2,subQ0]});Q6=makeQuery(id+"F40.imprint","IMPRINT",FACE,{"disambiguationData":[TD([[makeQuery(id+"F40.imprint","IMPRINT",EDGE,{"disambiguationData":[TD([[subQ3,-1.0]])],"derivedFrom":subQ0}),1.0]])]});}
            var Q7;
            {var subQ0=sQuery(id+"F40.wireOp",EDGE,"E193.15.0");var subQ1=sQuery(id+"F19.wireOp",EDGE,"E30");var subQ2=makeQuery(id+"F20.opRevolve","SWEPT_EDGE",EDGE,{"disambiguationData":[OSD([sQuery(id+"F19.wireOp",EDGE,"E29"),subQ1])]});var subQ3=makeQuery(id+"F40.imprint","INTERSECT",VERTEX,{"derivedFrom":[subQ2,subQ0]});Q7=makeQuery(id+"F40.imprint","IMPRINT",FACE,{"disambiguationData":[TD([[makeQuery(id+"F40.imprint","IMPRINT",EDGE,{"disambiguationData":[TD([[subQ3,-1.0]])],"derivedFrom":subQ0}),1.0]])]});}
            var Q8;
            {var subQ0=sQuery(id+"F40.wireOp",EDGE,"E193.13.0");var subQ1=sQuery(id+"F19.wireOp",EDGE,"E30");var subQ2=makeQuery(id+"F20.opRevolve","SWEPT_EDGE",EDGE,{"disambiguationData":[OSD([sQuery(id+"F19.wireOp",EDGE,"E29"),subQ1])]});var subQ3=makeQuery(id+"F40.imprint","INTERSECT",VERTEX,{"derivedFrom":[subQ2,subQ0]});Q8=makeQuery(id+"F40.imprint","IMPRINT",FACE,{"disambiguationData":[TD([[makeQuery(id+"F40.imprint","IMPRINT",EDGE,{"disambiguationData":[TD([[subQ3,-1.0]])],"derivedFrom":subQ0}),1.0]])]});}
            var Q9;
            {var subQ0=sQuery(id+"F40.wireOp",EDGE,"E193.11.0");var subQ1=sQuery(id+"F19.wireOp",EDGE,"E30");var subQ2=makeQuery(id+"F20.opRevolve","SWEPT_EDGE",EDGE,{"disambiguationData":[OSD([sQuery(id+"F19.wireOp",EDGE,"E29"),subQ1])]});var subQ3=makeQuery(id+"F40.imprint","INTERSECT",VERTEX,{"derivedFrom":[subQ2,subQ0]});Q9=makeQuery(id+"F40.imprint","IMPRINT",FACE,{"disambiguationData":[TD([[makeQuery(id+"F40.imprint","IMPRINT",EDGE,{"disambiguationData":[TD([[subQ3,-1.0]])],"derivedFrom":subQ0}),1.0]])]});}
            extrude(context, id + "F42", {"entities" : qUnion([Q0, Q1, Q2, Q3, Q4, Q5, Q6, Q7, Q8, Q9]), "operationType" : NewBodyOperationType.REMOVE, "oppositeDirection" : true, "depth" : 5 * mm, "offsetDistance" : 25 * mm, "hasDraft" : true, "draftAngle" : 45 * degree, "draftPullDirection" : true});
        }
        {
            var Q0;
            Q0=makeQuery(id+"F25.opRevolve","SWEPT_FACE",FACE,{"disambiguationData":[OSD([sQuery(id+"F24.wireOp",EDGE,"E105")])]});
            var sketch = newSketch(context, id + "F43", { "sketchPlane" : qUnion([Q0])});
            skLineSegment(sketch, "E215", {"start": v(-0.01, 0.04) * mm, "end": v(32.49, 0.04) * mm});
            skLineSegment(sketch, "E216.1.0", {"start": v(-0.01, 0.04) * mm, "end": v(19.02, 6.23) * mm});
            skLineSegment(sketch, "E216.2.0", {"start": v(-0.01, 0.04) * mm, "end": v(16.18, 11.8) * mm});
            skLineSegment(sketch, "E216.3.0", {"start": v(-0.01, 0.04) * mm, "end": v(19.09, 26.33) * mm});
            skLineSegment(sketch, "E216.4.0", {"start": v(-0.01, 0.04) * mm, "end": v(10.03, 30.95) * mm});
            skLineSegment(sketch, "E216.5.0", {"start": v(-0.01, 0.04) * mm, "end": v(-0.01, 32.54) * mm});
            skLineSegment(sketch, "E216.6.0", {"start": v(-0.01, 0.04) * mm, "end": v(-10.06, 30.95) * mm});
            skLineSegment(sketch, "E216.7.0", {"start": v(-0.01, 0.04) * mm, "end": v(-19.12, 26.33) * mm});
            skLineSegment(sketch, "E216.8.0", {"start": v(-0.01, 0.04) * mm, "end": v(-26.3, 19.14) * mm});
            skLineSegment(sketch, "E216.9.0", {"start": v(-0.01, 0.04) * mm, "end": v(-19.05, 6.23) * mm});
            skLineSegment(sketch, "E216.10.0", {"start": v(-0.01, 0.04) * mm, "end": v(-32.51, 0.04) * mm});
            skLineSegment(sketch, "E216.11.0", {"start": v(-0.01, 0.04) * mm, "end": v(-30.92, -10) * mm});
            skLineSegment(sketch, "E216.12.0", {"start": v(-0.01, 0.04) * mm, "end": v(-16.2, -11.72) * mm});
            skLineSegment(sketch, "E216.13.0", {"start": v(-0.01, 0.04) * mm, "end": v(-19.12, -26.25) * mm});
            skLineSegment(sketch, "E216.14.0", {"start": v(-0.01, 0.04) * mm, "end": v(-6.2, -19) * mm});
            skLineSegment(sketch, "E216.15.0", {"start": v(-0.01, 0.04) * mm, "end": v(-0.01, -19.97) * mm});
            skLineSegment(sketch, "E216.16.0", {"start": v(-0.01, 0.04) * mm, "end": v(6.17, -19) * mm});
            skLineSegment(sketch, "E216.17.0", {"start": v(-0.01, 0.04) * mm, "end": v(19.09, -26.25) * mm});
            skLineSegment(sketch, "E216.18.0", {"start": v(-0.01, 0.04) * mm, "end": v(16.18, -11.72) * mm});
            skLineSegment(sketch, "E216.19.0", {"start": v(-0.01, 0.04) * mm, "end": v(30.9, -10) * mm});
            skPoint(sketch, "E216.center", {"position": v(-0.01, 0.04) * mm});
            skCircle(sketch, "E217", {"center": v(-0.01, 0.04) * mm, "radius": 32.5 * mm});
            skArc(sketch, "E218", {"start": v(-16.2, 11.8) * mm, "mid": v(-19.05, 6.23) * mm, "end": v(-20.03, 0.04) * mm});
            skArc(sketch, "E219", {"start": v(-11.78, 16.23) * mm, "mid": v(-14.17, 14.2) * mm, "end": v(-16.2, 11.8) * mm});
            skArc(sketch, "E220", {"start": v(-6.2, 19.08) * mm, "mid": v(-9.1, 17.87) * mm, "end": v(-11.78, 16.23) * mm});
            skArc(sketch, "E221", {"start": v(-0.01, 20.06) * mm, "mid": v(-3.14, 19.81) * mm, "end": v(-6.2, 19.08) * mm});
            skArc(sketch, "E222", {"start": v(6.17, 19.08) * mm, "mid": v(3.12, 19.81) * mm, "end": v(-0.01, 20.06) * mm});
            skArc(sketch, "E223", {"start": v(11.75, 16.23) * mm, "mid": v(9.07, 17.87) * mm, "end": v(6.17, 19.08) * mm});
            skLineSegment(sketch, "E224", {"start": v(16.18, 11.8) * mm, "end": v(26.28, 19.14) * mm});
            skLineSegment(sketch, "E225", {"start": v(19.02, 6.23) * mm, "end": v(30.9, 10.08) * mm});
            skArc(sketch, "E226", {"start": v(20, 0.04) * mm, "mid": v(17.82, 9.13) * mm, "end": v(11.75, 16.23) * mm});
            skArc(sketch, "E227", {"start": v(19.02, -6.14) * mm, "mid": v(19.75, -3.09) * mm, "end": v(20, 0.04) * mm});
            skLineSegment(sketch, "E228", {"start": v(16.18, -11.72) * mm, "end": v(26.28, -19.06) * mm});
            skArc(sketch, "E229", {"start": v(11.75, -16.15) * mm, "mid": v(16.18, -11.72) * mm, "end": v(19.02, -6.14) * mm});
            skLineSegment(sketch, "E230", {"start": v(6.17, -19) * mm, "end": v(10.03, -30.87) * mm});
            skLineSegment(sketch, "E231", {"start": v(-0.01, -19.97) * mm, "end": v(-0.01, -32.46) * mm});
            skLineSegment(sketch, "E232", {"start": v(-6.2, -19) * mm, "end": v(-10.06, -30.87) * mm});
            skArc(sketch, "E233", {"start": v(-11.78, -16.15) * mm, "mid": v(-0.01, -19.97) * mm, "end": v(11.75, -16.15) * mm});
            skLineSegment(sketch, "E234", {"start": v(-16.2, -11.72) * mm, "end": v(-26.3, -19.06) * mm});
            skArc(sketch, "E235", {"start": v(-19.05, -6.14) * mm, "mid": v(-16.2, -11.72) * mm, "end": v(-11.78, -16.15) * mm});
            skArc(sketch, "E236", {"start": v(-20.03, 0.04) * mm, "mid": v(-19.78, -3.09) * mm, "end": v(-19.05, -6.14) * mm});
            skLineSegment(sketch, "E237", {"start": v(-19.05, 6.23) * mm, "end": v(-30.92, 10.08) * mm});
            skSolve(sketch);
        }
        {
            var Q0;
            {var subQ0=sQuery(id+"F43.wireOp",EDGE,"E215");var subQ1=sQuery(id+"F24.wireOp",EDGE,"E105");var subQ2=makeQuery(id+"F25.opRevolve","SWEPT_EDGE",EDGE,{"disambiguationData":[OSD([subQ1,sQuery(id+"F24.wireOp",EDGE,"E106")])]});var subQ3=makeQuery(id+"F43.imprint","INTERSECT",VERTEX,{"derivedFrom":[subQ2,subQ0]});Q0=makeQuery(id+"F43.imprint","IMPRINT",FACE,{"disambiguationData":[TD([[makeQuery(id+"F43.imprint","IMPRINT",EDGE,{"disambiguationData":[TD([[subQ3,-1.0]])],"derivedFrom":subQ0}),1.0]])]});}
            var Q1;
            {var subQ0=sQuery(id+"F43.wireOp",EDGE,"E216.2.0");var subQ1=sQuery(id+"F24.wireOp",EDGE,"E105");var subQ2=makeQuery(id+"F25.opRevolve","SWEPT_EDGE",EDGE,{"disambiguationData":[OSD([subQ1,sQuery(id+"F24.wireOp",EDGE,"E106")])]});var subQ3=makeQuery(id+"F43.imprint","INTERSECT",VERTEX,{"derivedFrom":[subQ2,subQ0]});Q1=makeQuery(id+"F43.imprint","IMPRINT",FACE,{"disambiguationData":[TD([[makeQuery(id+"F43.imprint","IMPRINT",EDGE,{"disambiguationData":[TD([[subQ3,-1.0]])],"derivedFrom":subQ0}),1.0]])]});}
            var Q2;
            {var subQ0=sQuery(id+"F43.wireOp",EDGE,"E216.4.0");var subQ1=sQuery(id+"F24.wireOp",EDGE,"E105");var subQ2=makeQuery(id+"F25.opRevolve","SWEPT_EDGE",EDGE,{"disambiguationData":[OSD([subQ1,sQuery(id+"F24.wireOp",EDGE,"E106")])]});var subQ3=makeQuery(id+"F43.imprint","INTERSECT",VERTEX,{"derivedFrom":[subQ2,subQ0]});Q2=makeQuery(id+"F43.imprint","IMPRINT",FACE,{"disambiguationData":[TD([[makeQuery(id+"F43.imprint","IMPRINT",EDGE,{"disambiguationData":[TD([[subQ3,-1.0]])],"derivedFrom":subQ0}),1.0]])]});}
            var Q3;
            {var subQ0=sQuery(id+"F43.wireOp",EDGE,"E216.6.0");var subQ1=sQuery(id+"F24.wireOp",EDGE,"E105");var subQ2=makeQuery(id+"F25.opRevolve","SWEPT_EDGE",EDGE,{"disambiguationData":[OSD([subQ1,sQuery(id+"F24.wireOp",EDGE,"E106")])]});var subQ3=makeQuery(id+"F43.imprint","INTERSECT",VERTEX,{"derivedFrom":[subQ2,subQ0]});Q3=makeQuery(id+"F43.imprint","IMPRINT",FACE,{"disambiguationData":[TD([[makeQuery(id+"F43.imprint","IMPRINT",EDGE,{"disambiguationData":[TD([[subQ3,-1.0]])],"derivedFrom":subQ0}),1.0]])]});}
            var Q4;
            {var subQ0=sQuery(id+"F43.wireOp",EDGE,"E216.8.0");var subQ1=sQuery(id+"F24.wireOp",EDGE,"E105");var subQ2=makeQuery(id+"F25.opRevolve","SWEPT_EDGE",EDGE,{"disambiguationData":[OSD([subQ1,sQuery(id+"F24.wireOp",EDGE,"E106")])]});var subQ3=makeQuery(id+"F43.imprint","INTERSECT",VERTEX,{"derivedFrom":[subQ2,subQ0]});Q4=makeQuery(id+"F43.imprint","IMPRINT",FACE,{"disambiguationData":[TD([[makeQuery(id+"F43.imprint","IMPRINT",EDGE,{"disambiguationData":[TD([[subQ3,-1.0]])],"derivedFrom":subQ0}),1.0]])]});}
            var Q5;
            {var subQ0=sQuery(id+"F43.wireOp",EDGE,"E216.10.0");var subQ1=sQuery(id+"F24.wireOp",EDGE,"E105");var subQ2=makeQuery(id+"F25.opRevolve","SWEPT_EDGE",EDGE,{"disambiguationData":[OSD([subQ1,sQuery(id+"F24.wireOp",EDGE,"E106")])]});var subQ3=makeQuery(id+"F43.imprint","INTERSECT",VERTEX,{"derivedFrom":[subQ2,subQ0]});Q5=makeQuery(id+"F43.imprint","IMPRINT",FACE,{"disambiguationData":[TD([[makeQuery(id+"F43.imprint","IMPRINT",EDGE,{"disambiguationData":[TD([[subQ3,-1.0]])],"derivedFrom":subQ0}),1.0]])]});}
            var Q6;
            {var subQ0=sQuery(id+"F43.wireOp",EDGE,"E216.12.0");var subQ1=sQuery(id+"F24.wireOp",EDGE,"E105");var subQ2=makeQuery(id+"F25.opRevolve","SWEPT_EDGE",EDGE,{"disambiguationData":[OSD([subQ1,sQuery(id+"F24.wireOp",EDGE,"E106")])]});var subQ3=makeQuery(id+"F43.imprint","INTERSECT",VERTEX,{"derivedFrom":[subQ2,subQ0]});Q6=makeQuery(id+"F43.imprint","IMPRINT",FACE,{"disambiguationData":[TD([[makeQuery(id+"F43.imprint","IMPRINT",EDGE,{"disambiguationData":[TD([[subQ3,-1.0]])],"derivedFrom":subQ0}),1.0]])]});}
            var Q7;
            {var subQ0=sQuery(id+"F43.wireOp",EDGE,"E216.14.0");var subQ1=sQuery(id+"F24.wireOp",EDGE,"E105");var subQ2=makeQuery(id+"F25.opRevolve","SWEPT_EDGE",EDGE,{"disambiguationData":[OSD([subQ1,sQuery(id+"F24.wireOp",EDGE,"E106")])]});var subQ3=makeQuery(id+"F43.imprint","INTERSECT",VERTEX,{"derivedFrom":[subQ2,subQ0]});Q7=makeQuery(id+"F43.imprint","IMPRINT",FACE,{"disambiguationData":[TD([[makeQuery(id+"F43.imprint","IMPRINT",EDGE,{"disambiguationData":[TD([[subQ3,-1.0]])],"derivedFrom":subQ0}),1.0]])]});}
            var Q8;
            {var subQ0=sQuery(id+"F43.wireOp",EDGE,"E216.16.0");var subQ1=sQuery(id+"F24.wireOp",EDGE,"E105");var subQ2=makeQuery(id+"F25.opRevolve","SWEPT_EDGE",EDGE,{"disambiguationData":[OSD([subQ1,sQuery(id+"F24.wireOp",EDGE,"E106")])]});var subQ3=makeQuery(id+"F43.imprint","INTERSECT",VERTEX,{"derivedFrom":[subQ2,subQ0]});Q8=makeQuery(id+"F43.imprint","IMPRINT",FACE,{"disambiguationData":[TD([[makeQuery(id+"F43.imprint","IMPRINT",EDGE,{"disambiguationData":[TD([[subQ3,-1.0]])],"derivedFrom":subQ0}),1.0]])]});}
            var Q9;
            {var subQ0=sQuery(id+"F43.wireOp",EDGE,"E216.18.0");var subQ1=sQuery(id+"F24.wireOp",EDGE,"E105");var subQ2=makeQuery(id+"F25.opRevolve","SWEPT_EDGE",EDGE,{"disambiguationData":[OSD([subQ1,sQuery(id+"F24.wireOp",EDGE,"E106")])]});var subQ3=makeQuery(id+"F43.imprint","INTERSECT",VERTEX,{"derivedFrom":[subQ2,subQ0]});Q9=makeQuery(id+"F43.imprint","IMPRINT",FACE,{"disambiguationData":[TD([[makeQuery(id+"F43.imprint","IMPRINT",EDGE,{"disambiguationData":[TD([[subQ3,-1.0]])],"derivedFrom":subQ0}),1.0]])]});}
            extrude(context, id + "F44", {"entities" : qUnion([Q0, Q1, Q2, Q3, Q4, Q5, Q6, Q7, Q8, Q9]), "operationType" : NewBodyOperationType.REMOVE, "oppositeDirection" : true, "depth" : 3 * mm, "offsetDistance" : 25 * mm, "hasDraft" : true, "draftAngle" : 45 * degree, "draftPullDirection" : true});
        }
        {
            var Q0;
            {var subQ0=sQuery(id+"F43.wireOp",EDGE,"E216.1.0");var subQ1=sQuery(id+"F24.wireOp",EDGE,"E105");var subQ2=makeQuery(id+"F25.opRevolve","SWEPT_EDGE",EDGE,{"disambiguationData":[OSD([subQ1,sQuery(id+"F24.wireOp",EDGE,"E106")])]});var subQ3=makeQuery(id+"F43.imprint","INTERSECT",VERTEX,{"derivedFrom":[subQ2,subQ0]});Q0=makeQuery(id+"F43.imprint","IMPRINT",FACE,{"disambiguationData":[TD([[makeQuery(id+"F43.imprint","IMPRINT",EDGE,{"disambiguationData":[TD([[subQ3,-1.0]])],"derivedFrom":subQ0}),1.0]])]});}
            var Q1;
            {var subQ0=sQuery(id+"F43.wireOp",EDGE,"E215");var subQ1=sQuery(id+"F24.wireOp",EDGE,"E105");var subQ2=makeQuery(id+"F25.opRevolve","SWEPT_EDGE",EDGE,{"disambiguationData":[OSD([subQ1,sQuery(id+"F24.wireOp",EDGE,"E106")])]});var subQ3=makeQuery(id+"F43.imprint","INTERSECT",VERTEX,{"derivedFrom":[subQ2,subQ0]});Q1=makeQuery(id+"F43.imprint","IMPRINT",FACE,{"disambiguationData":[TD([[makeQuery(id+"F43.imprint","IMPRINT",EDGE,{"disambiguationData":[TD([[subQ3,-1.0]])],"derivedFrom":subQ0}),-1.0]])]});}
            var Q2;
            {var subQ0=sQuery(id+"F43.wireOp",EDGE,"E216.17.0");var subQ1=sQuery(id+"F24.wireOp",EDGE,"E105");var subQ2=makeQuery(id+"F25.opRevolve","SWEPT_EDGE",EDGE,{"disambiguationData":[OSD([subQ1,sQuery(id+"F24.wireOp",EDGE,"E106")])]});var subQ3=makeQuery(id+"F43.imprint","INTERSECT",VERTEX,{"derivedFrom":[subQ2,subQ0]});Q2=makeQuery(id+"F43.imprint","IMPRINT",FACE,{"disambiguationData":[TD([[makeQuery(id+"F43.imprint","IMPRINT",EDGE,{"disambiguationData":[TD([[subQ3,-1.0]])],"derivedFrom":subQ0}),1.0]])]});}
            var Q3;
            {var subQ0=sQuery(id+"F43.wireOp",EDGE,"E216.15.0");var subQ1=sQuery(id+"F24.wireOp",EDGE,"E105");var subQ2=makeQuery(id+"F25.opRevolve","SWEPT_EDGE",EDGE,{"disambiguationData":[OSD([subQ1,sQuery(id+"F24.wireOp",EDGE,"E106")])]});var subQ3=makeQuery(id+"F43.imprint","INTERSECT",VERTEX,{"derivedFrom":[subQ2,subQ0]});Q3=makeQuery(id+"F43.imprint","IMPRINT",FACE,{"disambiguationData":[TD([[makeQuery(id+"F43.imprint","IMPRINT",EDGE,{"disambiguationData":[TD([[subQ3,-1.0]])],"derivedFrom":subQ0}),1.0]])]});}
            var Q4;
            {var subQ0=sQuery(id+"F43.wireOp",EDGE,"E216.13.0");var subQ1=sQuery(id+"F24.wireOp",EDGE,"E105");var subQ2=makeQuery(id+"F25.opRevolve","SWEPT_EDGE",EDGE,{"disambiguationData":[OSD([subQ1,sQuery(id+"F24.wireOp",EDGE,"E106")])]});var subQ3=makeQuery(id+"F43.imprint","INTERSECT",VERTEX,{"derivedFrom":[subQ2,subQ0]});Q4=makeQuery(id+"F43.imprint","IMPRINT",FACE,{"disambiguationData":[TD([[makeQuery(id+"F43.imprint","IMPRINT",EDGE,{"disambiguationData":[TD([[subQ3,-1.0]])],"derivedFrom":subQ0}),1.0]])]});}
            var Q5;
            {var subQ0=sQuery(id+"F43.wireOp",EDGE,"E216.11.0");var subQ1=sQuery(id+"F24.wireOp",EDGE,"E105");var subQ2=makeQuery(id+"F25.opRevolve","SWEPT_EDGE",EDGE,{"disambiguationData":[OSD([subQ1,sQuery(id+"F24.wireOp",EDGE,"E106")])]});var subQ3=makeQuery(id+"F43.imprint","INTERSECT",VERTEX,{"derivedFrom":[subQ2,subQ0]});Q5=makeQuery(id+"F43.imprint","IMPRINT",FACE,{"disambiguationData":[TD([[makeQuery(id+"F43.imprint","IMPRINT",EDGE,{"disambiguationData":[TD([[subQ3,-1.0]])],"derivedFrom":subQ0}),1.0]])]});}
            var Q6;
            {var subQ0=sQuery(id+"F43.wireOp",EDGE,"E216.9.0");var subQ1=sQuery(id+"F24.wireOp",EDGE,"E105");var subQ2=makeQuery(id+"F25.opRevolve","SWEPT_EDGE",EDGE,{"disambiguationData":[OSD([subQ1,sQuery(id+"F24.wireOp",EDGE,"E106")])]});var subQ3=makeQuery(id+"F43.imprint","INTERSECT",VERTEX,{"derivedFrom":[subQ2,subQ0]});Q6=makeQuery(id+"F43.imprint","IMPRINT",FACE,{"disambiguationData":[TD([[makeQuery(id+"F43.imprint","IMPRINT",EDGE,{"disambiguationData":[TD([[subQ3,-1.0]])],"derivedFrom":subQ0}),1.0]])]});}
            var Q7;
            {var subQ0=sQuery(id+"F43.wireOp",EDGE,"E216.7.0");var subQ1=sQuery(id+"F24.wireOp",EDGE,"E105");var subQ2=makeQuery(id+"F25.opRevolve","SWEPT_EDGE",EDGE,{"disambiguationData":[OSD([subQ1,sQuery(id+"F24.wireOp",EDGE,"E106")])]});var subQ3=makeQuery(id+"F43.imprint","INTERSECT",VERTEX,{"derivedFrom":[subQ2,subQ0]});Q7=makeQuery(id+"F43.imprint","IMPRINT",FACE,{"disambiguationData":[TD([[makeQuery(id+"F43.imprint","IMPRINT",EDGE,{"disambiguationData":[TD([[subQ3,-1.0]])],"derivedFrom":subQ0}),1.0]])]});}
            var Q8;
            {var subQ0=sQuery(id+"F43.wireOp",EDGE,"E216.5.0");var subQ1=sQuery(id+"F24.wireOp",EDGE,"E105");var subQ2=makeQuery(id+"F25.opRevolve","SWEPT_EDGE",EDGE,{"disambiguationData":[OSD([subQ1,sQuery(id+"F24.wireOp",EDGE,"E106")])]});var subQ3=makeQuery(id+"F43.imprint","INTERSECT",VERTEX,{"derivedFrom":[subQ2,subQ0]});Q8=makeQuery(id+"F43.imprint","IMPRINT",FACE,{"disambiguationData":[TD([[makeQuery(id+"F43.imprint","IMPRINT",EDGE,{"disambiguationData":[TD([[subQ3,-1.0]])],"derivedFrom":subQ0}),1.0]])]});}
            var Q9;
            {var subQ0=sQuery(id+"F43.wireOp",EDGE,"E216.3.0");var subQ1=sQuery(id+"F24.wireOp",EDGE,"E105");var subQ2=makeQuery(id+"F25.opRevolve","SWEPT_EDGE",EDGE,{"disambiguationData":[OSD([subQ1,sQuery(id+"F24.wireOp",EDGE,"E106")])]});var subQ3=makeQuery(id+"F43.imprint","INTERSECT",VERTEX,{"derivedFrom":[subQ2,subQ0]});Q9=makeQuery(id+"F43.imprint","IMPRINT",FACE,{"disambiguationData":[TD([[makeQuery(id+"F43.imprint","IMPRINT",EDGE,{"disambiguationData":[TD([[subQ3,-1.0]])],"derivedFrom":subQ0}),1.0]])]});}
            extrude(context, id + "F45", {"entities" : qUnion([Q0, Q1, Q2, Q3, Q4, Q5, Q6, Q7, Q8, Q9]), "operationType" : NewBodyOperationType.REMOVE, "oppositeDirection" : true, "depth" : 3 * mm, "offsetDistance" : 25 * mm, "hasDraft" : true, "draftAngle" : 45 * degree, "draftPullDirection" : true});
        }
        {
            var Q0;
            Q0=makeQuery(id+"F29.imprint","IMPRINT",FACE,{"disambiguationData":[TD([[makeQuery(id+"F29.imprint","IMPRINT",EDGE,{"derivedFrom":sQuery(id+"F29.wireOp",EDGE,"E137")}),-1.0]])]});
            var Q1;
            Q1=makeQuery(id+"F29.imprint","IMPRINT",FACE,{"disambiguationData":[TD([[makeQuery(id+"F29.imprint","IMPRINT",EDGE,{"derivedFrom":sQuery(id+"F29.wireOp",EDGE,"E135")}),-1.0]])]});
            var Q2;
            Q2=makeQuery(id+"F29.imprint","IMPRINT",FACE,{"disambiguationData":[TD([[makeQuery(id+"F29.imprint","IMPRINT",EDGE,{"derivedFrom":sQuery(id+"F29.wireOp",EDGE,"E138")}),1.0]])]});
            extrude(context, id + "F46", {"entities" : qUnion([Q0, Q1, Q2]), "operationType" : NewBodyOperationType.REMOVE, "oppositeDirection" : true, "depth" : 5 * mm, "offsetDistance" : 25 * mm, "hasDraft" : true, "draftAngle" : 45 * degree, "draftPullDirection" : true});
        }
        {
            var Q0;
            Q0=makeQuery(id+"F29.imprint","IMPRINT",FACE,{"disambiguationData":[TD([[makeQuery(id+"F29.imprint","IMPRINT",EDGE,{"derivedFrom":sQuery(id+"F29.wireOp",EDGE,"E136")}),-1.0]])]});
            var Q1;
            Q1=makeQuery(id+"F29.imprint","IMPRINT",FACE,{"disambiguationData":[TD([[makeQuery(id+"F29.imprint","IMPRINT",EDGE,{"derivedFrom":sQuery(id+"F29.wireOp",EDGE,"E135")}),1.0]])]});
            extrude(context, id + "F47", {"entities" : qUnion([Q0, Q1]), "operationType" : NewBodyOperationType.REMOVE, "oppositeDirection" : true, "depth" : 25 * mm, "offsetDistance" : 25 * mm, "hasDraft" : true, "draftAngle" : 45 * degree, "draftPullDirection" : true});
        }
        {
            var Q0;
            Q0=makeQuery(id+"F36.boolean.opBoolean","SPLIT",FACE,{"disambiguationData":[TD([makeQuery(id+"F18.opRevolve","SWEPT_FACE",FACE,{"disambiguationData":[OSD([sQuery(id+"F17.wireOp",EDGE,"E14")])]})])],"derivedFrom":makeQuery(id+"F18.opRevolve","SWEPT_FACE",FACE,{"disambiguationData":[OSD([sQuery(id+"F17.wireOp",EDGE,"E13")])]})});
            var sketch = newSketch(context, id + "F48", { "sketchPlane" : qUnion([Q0])});
            skCircle(sketch, "E238", {"center": v(0, 0) * mm, "radius": 25.31 * mm});
            skCircle(sketch, "E239", {"center": v(0, 0) * mm, "radius": 29.93 * mm});
            skCircle(sketch, "E240", {"center": v(0, 0) * mm, "radius": 35.5 * mm});
            skCircle(sketch, "E241", {"center": v(0, 0) * mm, "radius": 20.2 * mm});
            skSolve(sketch);
        }
        {
            var Q0;
            Q0=makeQuery(id+"F48.imprint","IMPRINT",FACE,{"disambiguationData":[TD([[makeQuery(id+"F48.imprint","IMPRINT",EDGE,{"derivedFrom":sQuery(id+"F48.wireOp",EDGE,"E238")}),1.0]])]});
            var Q1;
            Q1=makeQuery(id+"F48.imprint","IMPRINT",FACE,{"disambiguationData":[TD([[makeQuery(id+"F48.imprint","IMPRINT",EDGE,{"derivedFrom":sQuery(id+"F48.wireOp",EDGE,"E239")}),-1.0]])]});
            extrude(context, id + "F49", {"entities" : qUnion([Q0, Q1]), "operationType" : NewBodyOperationType.REMOVE, "oppositeDirection" : true, "depth" : 5 * mm, "offsetDistance" : 25 * mm, "hasDraft" : true, "draftAngle" : 45 * degree, "draftPullDirection" : true});
        }
        {
            var Q0;
            Q0=makeQuery(id+"F48.imprint","IMPRINT",FACE,{"disambiguationData":[TD([[makeQuery(id+"F48.imprint","IMPRINT",EDGE,{"derivedFrom":sQuery(id+"F48.wireOp",EDGE,"E238")}),-1.0]])]});
            extrude(context, id + "F50", {"entities" : qUnion([Q0]), "operationType" : NewBodyOperationType.REMOVE, "oppositeDirection" : true, "depth" : 25 * mm, "offsetDistance" : 25 * mm, "hasDraft" : true, "draftAngle" : 45 * degree, "draftPullDirection" : true});
        }
        {
            var Q0;
            Q0=makeQuery(id+"F30.imprint","IMPRINT",FACE,{"disambiguationData":[TD([[makeQuery(id+"F30.imprint","IMPRINT",EDGE,{"derivedFrom":sQuery(id+"F30.wireOp",EDGE,"E139")}),1.0]])]});
            var Q1;
            Q1=makeQuery(id+"F30.imprint","IMPRINT",FACE,{"disambiguationData":[TD([[makeQuery(id+"F30.imprint","IMPRINT",EDGE,{"derivedFrom":sQuery(id+"F30.wireOp",EDGE,"E140")}),1.0]])]});
            extrude(context, id + "F51", {"entities" : qUnion([Q0, Q1]), "operationType" : NewBodyOperationType.REMOVE, "oppositeDirection" : true, "depth" : 25 * mm, "offsetDistance" : 25 * mm, "hasDraft" : true, "draftAngle" : 45 * degree, "draftPullDirection" : true});
        }
        {
            var Q0;
            Q0=makeQuery(id+"F30.imprint","IMPRINT",FACE,{"disambiguationData":[TD([[makeQuery(id+"F30.imprint","IMPRINT",EDGE,{"derivedFrom":sQuery(id+"F30.wireOp",EDGE,"E139")}),-1.0]])]});
            var Q1;
            Q1=makeQuery(id+"F30.imprint","IMPRINT",FACE,{"disambiguationData":[TD([[makeQuery(id+"F30.imprint","IMPRINT",EDGE,{"derivedFrom":sQuery(id+"F30.wireOp",EDGE,"E140")}),-1.0]])]});
            var Q2;
            Q2=makeQuery(id+"F30.imprint","IMPRINT",FACE,{"disambiguationData":[TD([[makeQuery(id+"F30.imprint","IMPRINT",EDGE,{"derivedFrom":sQuery(id+"F30.wireOp",EDGE,"E141")}),1.0]])]});
            extrude(context, id + "F52", {"entities" : qUnion([Q0, Q1, Q2]), "operationType" : NewBodyOperationType.REMOVE, "oppositeDirection" : true, "depth" : 25 * mm, "offsetDistance" : 25 * mm, "hasDraft" : true, "draftAngle" : 45 * degree, "draftPullDirection" : true});
        }
        {
            var Q0;
            Q0=makeQuery(id+"F31.imprint","IMPRINT",FACE,{"disambiguationData":[TD([[makeQuery(id+"F31.imprint","IMPRINT",EDGE,{"derivedFrom":sQuery(id+"F31.wireOp",EDGE,"E143")}),1.0]])]});
            var Q1;
            Q1=makeQuery(id+"F31.imprint","IMPRINT",FACE,{"disambiguationData":[TD([[makeQuery(id+"F31.imprint","IMPRINT",EDGE,{"derivedFrom":sQuery(id+"F31.wireOp",EDGE,"E144")}),-1.0]])]});
            var Q2;
            Q2=makeQuery(id+"F31.imprint","IMPRINT",FACE,{"disambiguationData":[TD([[makeQuery(id+"F31.imprint","IMPRINT",EDGE,{"derivedFrom":sQuery(id+"F31.wireOp",EDGE,"E145")}),1.0]])]});
            extrude(context, id + "F53", {"entities" : qUnion([Q0, Q1, Q2]), "operationType" : NewBodyOperationType.REMOVE, "oppositeDirection" : true, "depth" : 25 * mm, "offsetDistance" : 25 * mm, "hasDraft" : true, "draftAngle" : 45 * degree, "draftPullDirection" : true});
        }
        {
            var Q0;
            Q0=makeQuery(id+"F31.imprint","IMPRINT",FACE,{"disambiguationData":[TD([[makeQuery(id+"F31.imprint","IMPRINT",EDGE,{"derivedFrom":sQuery(id+"F31.wireOp",EDGE,"E143")}),-1.0]])]});
            extrude(context, id + "F54", {"entities" : qUnion([Q0]), "operationType" : NewBodyOperationType.REMOVE, "oppositeDirection" : true, "depth" : 25 * mm, "offsetDistance" : 25 * mm, "hasDraft" : true, "draftAngle" : 45 * degree, "draftPullDirection" : true});
        }
        {
            var Q0;
            Q0=makeQuery(id+"F27.imprint","IMPRINT",FACE,{"disambiguationData":[TD([[makeQuery(id+"F27.imprint","IMPRINT",EDGE,{"derivedFrom":sQuery(id+"F27.wireOp",EDGE,"E109")}),1.0]])]});
            var Q1;
            Q1=makeQuery(id+"F27.imprint","IMPRINT",FACE,{"disambiguationData":[TD([[makeQuery(id+"F27.imprint","IMPRINT",EDGE,{"derivedFrom":sQuery(id+"F27.wireOp",EDGE,"E110")}),-1.0]])]});
            var Q2;
            Q2=makeQuery(id+"F27.imprint","IMPRINT",FACE,{"disambiguationData":[TD([[makeQuery(id+"F27.imprint","IMPRINT",EDGE,{"derivedFrom":sQuery(id+"F27.wireOp",EDGE,"E111")}),1.0]])]});
            extrude(context, id + "F55", {"entities" : qUnion([Q0, Q1, Q2]), "operationType" : NewBodyOperationType.REMOVE, "oppositeDirection" : true, "depth" : 5 * mm, "offsetDistance" : 25 * mm, "hasDraft" : true, "draftAngle" : 45 * degree, "draftPullDirection" : true});
        }
        {
            var Q0;
            Q0=makeQuery(id+"F27.imprint","IMPRINT",FACE,{"disambiguationData":[TD([[makeQuery(id+"F27.imprint","IMPRINT",EDGE,{"derivedFrom":sQuery(id+"F27.wireOp",EDGE,"E109")}),-1.0]])]});
            extrude(context, id + "F56", {"entities" : qUnion([Q0]), "operationType" : NewBodyOperationType.REMOVE, "oppositeDirection" : true, "depth" : 5 * mm, "offsetDistance" : 25 * mm, "hasDraft" : true, "draftAngle" : 45 * degree, "draftPullDirection" : true});
        }
        {
            var Q0;
            Q0=makeQuery(id+"F0.imprint","IMPRINT",FACE,{"disambiguationData":[TD([[makeQuery(id+"F0.imprint","IMPRINT",EDGE,{"derivedFrom":sQuery(id+"F0.wireOp",EDGE,"E0.bottom")}),-1.0]])]});
            var sketch = newSketch(context, id + "F57", { "sketchPlane" : qUnion([Q0])});
            skCircle(sketch, "E242.cCircle", {"center": v(38, 0) * mm, "radius": 1.5 * mm, "construction": true});
            skLineSegment(sketch, "E242.0", {"start": v(39.5, 2.6) * mm, "end": v(39.5, -2.6) * mm});
            skLineSegment(sketch, "E242.1", {"start": v(39.5, -2.6) * mm, "end": v(35, 0) * mm});
            skLineSegment(sketch, "E242.2", {"start": v(35, 0) * mm, "end": v(39.5, 2.6) * mm});
            skPoint(sketch, "E242.0.midPoint", {"position": v(39.5, 0) * mm});
            skSolve(sketch);
        }
        {
            var Q0;
            Q0=qSketchRegion(id+"F57",true);
            extrude(context, id + "F58", {"entities" : qUnion([Q0]), "operationType" : NewBodyOperationType.REMOVE, "oppositeDirection" : true, "depth" : 1 * mm, "offsetDistance" : 25 * mm});
        }
    });
